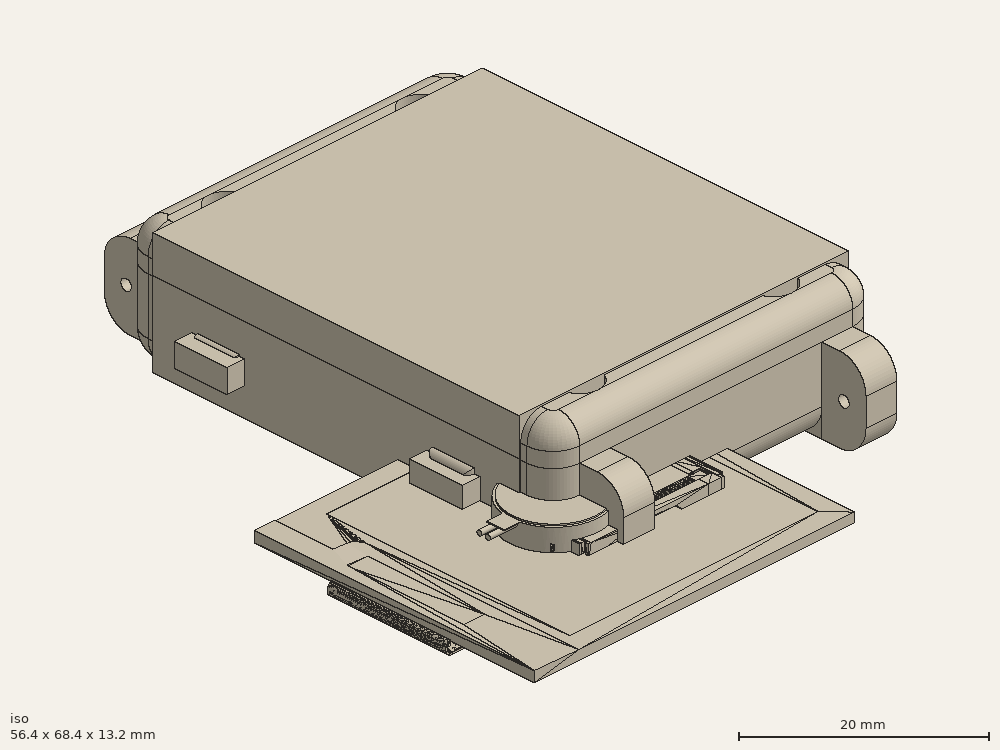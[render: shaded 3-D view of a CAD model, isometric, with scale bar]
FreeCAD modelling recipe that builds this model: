
FCSTD DOCUMENT  (FreeCAD 0.20R29177 +426 (Git))
Label: JJ-WATCHY_X
License: All rights reserved
LicenseURL: http://en.wikipedia.org/wiki/All_rights_reserved
objects: Part::Feature×73, App::Part×71, Sketcher::SketchObject×44, PartDesign::Pad×29, PartDesign::Pocket×23, PartDesign::ShapeBinder×11, PartDesign::Fillet×10, PartDesign::Body×8, PartDesign::Plane×4, Part::Part2DObjectPython×1, Part::Extrusion×1, PartDesign::FeatureBase×1, Mesh::Feature×1, Part::Fuse×1, Part::Cut×1
note: 269 computed .brp shape members not serialized (recipe doc carries the construction recipe); baked Part::Feature solids carry a one-line shape summary decoded from their .brp

FEATURE [Part::Feature] Part__Feature  label="SOLID (15)"
  shape: bbox 7.981 x 5.422 x 2.941 mm, 498 faces (baked)
FEATURE [App::Part] USB_Micro_B_Molex_47346_0001  label="USB_Micro-B_Molex_47346-0001"
  Group = -> [Part__Feature]
  Origin = -> Origin
  Placement = pos=(31.38,22.43,1.65) rot=(0,0,1;1.5708rad)
FEATURE [Part::Feature] Part__Feature001  label="SOLID"
  shape: bbox 1.6 x 0.8 x 0.8 mm, 28 faces (baked)
FEATURE [App::Part] C_0603_1608Metric
  Group = -> [Part__Feature001]
  Origin = -> Origin001
  Placement = pos=(5.16,37.71,1.65) rot=(0,0,1;0rad)
FEATURE [Part::Feature] Part__Feature002  label="SOLID (16)"
  shape: bbox 6.669 x 4.906 x 2.452 mm, 452 faces (baked)
FEATURE [App::Part] Button
  Group = -> [Part__Feature002]
  Origin = -> Origin002
  Placement = pos=(2.38,35.43,1.65) rot=(0,0,-1;1.5708rad)
FEATURE [Part::Feature] Part__Feature003  label="SOLID (16)001"
  shape: bbox 6.669 x 4.906 x 2.452 mm, 452 faces (baked)
FEATURE [App::Part] Button001
  Group = -> [Part__Feature003]
  Origin = -> Origin003
  Placement = pos=(2.38,8.73,1.65) rot=(0,0,-1;1.5708rad)
FEATURE [Part::Feature] Part__Feature004  label="SOLID (16)002"
  shape: bbox 6.669 x 4.906 x 2.452 mm, 452 faces (baked)
FEATURE [App::Part] Button002
  Group = -> [Part__Feature004]
  Origin = -> Origin004
  Placement = pos=(31.42,37.23,1.65) rot=(0,0,1;1.5708rad)
FEATURE [Part::Feature] Part__Feature005  label="SOLID (16)003"
  shape: bbox 6.669 x 4.906 x 2.452 mm, 452 faces (baked)
FEATURE [App::Part] Button003
  Group = -> [Part__Feature005]
  Origin = -> Origin005
  Placement = pos=(31.42,10.53,1.65) rot=(0,0,1;1.5708rad)
FEATURE [Part::Feature] Part__Feature006  label="SOLID (1)"
  shape: bbox 2 x 2 x 1.025 mm, 68 faces (baked)
FEATURE [App::Part] LGA_12_2x2mm_P0_5mm  label="LGA-12_2x2mm_P0.5mm"
  Group = -> [Part__Feature006]
  Origin = -> Origin006
  Placement = pos=(10.76,34.89,1.65) rot=(0,0,1;3.14159rad)
FEATURE [Part::Feature] Part__Feature007  label="COMPOUND (3)"
  shape: bbox 16.3 x 5.85 x 2.11 mm, 1280 faces, 17 solids (baked)
FEATURE [App::Part] FPC_24  label="FPC-24"
  Group = -> [Part__Feature007]
  Origin = -> Origin007
  Placement = pos=(11.025,19.09,1.65) rot=(0,0,1;0rad)
FEATURE [Part::Feature] Part__Feature008  label="SOLID (4)"
  shape: bbox 7.65 x 5.2 x 3.4 mm, 136 faces (baked)
FEATURE [App::Part] Molex_PicoBlade_53261_0271_1x02_1MP_P1_25mm_Horizontal  label="Molex_PicoBlade_53261-0271_1x02-1MP_P1.25mm_Horizontal"
  Group = -> [Part__Feature008]
  Origin = -> Origin008
  Placement = pos=(28.63,31.39,1.65) rot=(0,0,-1;1.5708rad)
FEATURE [Part::Feature] Part__Feature009  label="SOLID (2)"
  shape: bbox 1 x 0.5 x 0.35 mm, 26 faces (baked)
FEATURE [App::Part] R_0402_1005Metric
  Group = -> [Part__Feature009]
  Origin = -> Origin009
  Placement = pos=(31.7,28.28,1.65) rot=(0,0,1;1.5708rad)
FEATURE [Part::Feature] Part__Feature010  label="SOLID (5)"
  shape: bbox 4 x 4 x 1.1 mm, 158 faces (baked)
FEATURE [App::Part] QFN_24_1EP_4x4mm_P0_5mm_EP2_7x2_7mm  label="QFN-24-1EP_4x4mm_P0.5mm_EP2.7x2.7mm"
  Group = -> [Part__Feature010]
  Origin = -> Origin010
  Placement = pos=(25.76,24.38,1.65) rot=(0,0,1;0rad)
FEATURE [Part::Feature] Part__Feature011  label="SOLID (2)001"
  shape: bbox 1 x 0.5 x 0.35 mm, 26 faces (baked)
FEATURE [App::Part] R_0402_1005Metric001
  Group = -> [Part__Feature011]
  Origin = -> Origin011
  Placement = pos=(29.05,13.07,1.65) rot=(0,0,1;0rad)
FEATURE [Part::Feature] Part__Feature012  label="SOLID001"
  shape: bbox 1.6 x 0.8 x 0.8 mm, 28 faces (baked)
FEATURE [App::Part] C_0603_1608Metric001
  Group = -> [Part__Feature012]
  Origin = -> Origin012
  Placement = pos=(21.71,23.42,1.65) rot=(0,0,1;0rad)
FEATURE [Part::Feature] Part__Feature013  label="COMPOUND"
  shape: bbox 37.16 x 32.08 x 2.7 mm, 57 faces, 2 solids (baked)
FEATURE [App::Part] Display
  Group = -> [Part__Feature013]
  Origin = -> Origin013
  Placement = pos=(16.89,23.15,0.55) rot=(0.707107,0.707107,0;3.14159rad)
FEATURE [Part::Feature] Part__Feature014  label="SOLID002"
  shape: bbox 1.6 x 0.8 x 0.8 mm, 28 faces (baked)
FEATURE [App::Part] C_0603_1608Metric002
  Group = -> [Part__Feature014]
  Origin = -> Origin014
  Placement = pos=(15.42,35.06,1.65) rot=(0,0,1;1.5708rad)
FEATURE [Part::Feature] Part__Feature015  label="SOLID003"
  shape: bbox 1.6 x 0.8 x 0.8 mm, 28 faces (baked)
FEATURE [App::Part] C_0603_1608Metric003
  Group = -> [Part__Feature015]
  Origin = -> Origin015
  Placement = pos=(19.01,21.47,1.65) rot=(0,0,1;1.5708rad)
FEATURE [Part::Feature] Part__Feature016  label="SOLID (3)"
  shape: bbox 2 x 1.25 x 1.25 mm, 28 faces (baked)
FEATURE [App::Part] C_0805_2012Metric
  Group = -> [Part__Feature016]
  Origin = -> Origin016
  Placement = pos=(5.63,12.59,1.65) rot=(0,0,1;0rad)
FEATURE [Part::Feature] Part__Feature017  label="SOLID (3)001"
  shape: bbox 2 x 1.25 x 1.25 mm, 28 faces (baked)
FEATURE [App::Part] C_0805_2012Metric001
  Group = -> [Part__Feature017]
  Origin = -> Origin017
  Placement = pos=(6.63,6.34,1.65) rot=(0,0,1;0rad)
FEATURE [Part::Feature] Part__Feature018  label="SOLID004"
  shape: bbox 1.6 x 0.8 x 0.8 mm, 28 faces (baked)
FEATURE [App::Part] C_0603_1608Metric004
  Group = -> [Part__Feature018]
  Origin = -> Origin018
  Placement = pos=(13.81,21.47,1.65) rot=(0,0,1;1.5708rad)
FEATURE [Part::Feature] Part__Feature019  label="SOLID005"
  shape: bbox 1.6 x 0.8 x 0.8 mm, 28 faces (baked)
FEATURE [App::Part] C_0603_1608Metric005
  Group = -> [Part__Feature019]
  Origin = -> Origin019
  Placement = pos=(16.41,21.47,1.65) rot=(0,0,1;1.5708rad)
FEATURE [Part::Feature] Part__Feature020  label="SOLID006"
  shape: bbox 1.6 x 0.8 x 0.8 mm, 28 faces (baked)
FEATURE [App::Part] C_0603_1608Metric006
  Group = -> [Part__Feature020]
  Origin = -> Origin020
  Placement = pos=(17.71,21.47,1.65) rot=(0,0,1;1.5708rad)
FEATURE [Part::Feature] Part__Feature021  label="SOLID007"
  shape: bbox 1.6 x 0.8 x 0.8 mm, 28 faces (baked)
FEATURE [App::Part] C_0603_1608Metric007
  Group = -> [Part__Feature021]
  Origin = -> Origin021
  Placement = pos=(15.11,21.47,1.65) rot=(0,0,1;1.5708rad)
FEATURE [Part::Feature] Part__Feature022  label="SOLID008"
  shape: bbox 1.6 x 0.8 x 0.8 mm, 28 faces (baked)
FEATURE [App::Part] C_0603_1608Metric008
  Group = -> [Part__Feature022]
  Origin = -> Origin022
  Placement = pos=(12.46,21.47,1.65) rot=(0,0,1;1.5708rad)
FEATURE [Part::Feature] Part__Feature023  label="SOLID009"
  shape: bbox 1.6 x 0.8 x 0.8 mm, 28 faces (baked)
FEATURE [App::Part] C_0603_1608Metric009
  Group = -> [Part__Feature023]
  Origin = -> Origin023
  Placement = pos=(11.16,21.47,1.65) rot=(0,0,1;1.5708rad)
FEATURE [Part::Feature] Part__Feature024  label="SOLID (3)002"
  shape: bbox 2 x 1.25 x 1.25 mm, 28 faces (baked)
FEATURE [App::Part] C_0805_2012Metric002
  Group = -> [Part__Feature024]
  Origin = -> Origin024
  Placement = pos=(17.82,35.53,1.65) rot=(0,0,1;3.14159rad)
FEATURE [Part::Feature] Part__Feature025  label="SOLID (6)"
  shape: bbox 3.8 x 1.6 x 1.25 mm, 67 faces (baked)
FEATURE [App::Part] D_SOD_123  label="D_SOD-123"
  Group = -> [Part__Feature025]
  Origin = -> Origin025
  Placement = pos=(1.25,15.82,1.65) rot=(0,0,1;1.5708rad)
FEATURE [Part::Feature] Part__Feature026  label="SOLID (6)001"
  shape: bbox 3.8 x 1.6 x 1.25 mm, 67 faces (baked)
FEATURE [App::Part] D_SOD_123001  label="D_SOD-124"
  Group = -> [Part__Feature026]
  Origin = -> Origin026
  Placement = pos=(3.55,15.82,1.65) rot=(0,0,-1;1.5708rad)
FEATURE [Part::Feature] Part__Feature027  label="SOLID (6)002"
  shape: bbox 3.8 x 1.6 x 1.25 mm, 67 faces (baked)
FEATURE [App::Part] D_SOD_123002  label="D_SOD-125"
  Group = -> [Part__Feature027]
  Origin = -> Origin027
  Placement = pos=(5.85,15.82,1.65) rot=(0,0,-1;1.5708rad)
FEATURE [Part::Feature] Part__Feature028  label="SOLID (6)003"
  shape: bbox 3.8 x 1.6 x 1.25 mm, 67 faces (baked)
FEATURE [App::Part] D_SOD_123003  label="D_SOD-126"
  Group = -> [Part__Feature028]
  Origin = -> Origin028
  Placement = pos=(27.27,19.28,1.65) rot=(0,0,1;1.5708rad)
FEATURE [Part::Feature] Part__Feature029  label="SOLID (7)"
  shape: bbox 1.6 x 0.8 x 1.1 mm, 50 faces (baked)
FEATURE [App::Part] LED_0603_1608Metric
  Group = -> [Part__Feature029]
  Origin = -> Origin029
  Placement = pos=(33.04,30.53,1.65) rot=(0,0,1;1.5708rad)
FEATURE [Part::Feature] Part__Feature030  label="SOLID (8)"
  shape: bbox 3.5 x 1.6 x 1.1 mm, 27 faces (baked)
FEATURE [App::Part] D_SOD_123F  label="D_SOD-123F"
  Group = -> [Part__Feature030]
  Origin = -> Origin030
  Placement = pos=(4.91,34.705,1.65) rot=(0,0,-1;1.5708rad)
FEATURE [Part::Feature] Part__Feature031  label="SOLID (9)"
  shape: bbox 3.2 x 2.5 x 2.5 mm, 28 faces (baked)
FEATURE [App::Part] L_1210_3225Metric
  Group = -> [Part__Feature031]
  Origin = -> Origin031
  Placement = pos=(6.13,9.47,1.65) rot=(0,0,-1;1.5708rad)
FEATURE [Part::Feature] Part__Feature032  label="SOLID (10)"
  shape: bbox 2.5 x 3 x 1.2 mm, 76 faces (baked)
FEATURE [App::Part] SOT_23  label="SOT-23"
  Group = -> [Part__Feature032]
  Origin = -> Origin032
  Placement = pos=(28.1,9.03,1.65) rot=(0,0,-1;1.5708rad)
FEATURE [Part::Feature] Part__Feature033  label="SOLID (10)001"
  shape: bbox 2.5 x 3 x 1.2 mm, 76 faces (baked)
FEATURE [App::Part] SOT_23001  label="SOT-024"
  Group = -> [Part__Feature033]
  Origin = -> Origin033
  Placement = pos=(28.45,15.23,1.65) rot=(0,0,-1;1.5708rad)
FEATURE [Part::Feature] Part__Feature034  label="SOLID (10)002"
  shape: bbox 2.5 x 3 x 1.2 mm, 76 faces (baked)
FEATURE [App::Part] SOT_23002  label="SOT-025"
  Group = -> [Part__Feature034]
  Origin = -> Origin034
  Placement = pos=(7.81,35.31,1.65) rot=(0,0,1;3.14159rad)
FEATURE [Part::Feature] Part__Feature035  label="SOLID (2)002"
  shape: bbox 1 x 0.5 x 0.35 mm, 26 faces (baked)
FEATURE [App::Part] R_0402_1005Metric002
  Group = -> [Part__Feature035]
  Origin = -> Origin035
  Placement = pos=(16.97,34.19,1.65) rot=(0,0,1;3.14159rad)
FEATURE [Part::Feature] Part__Feature036  label="SOLID (2)003"
  shape: bbox 1 x 0.5 x 0.35 mm, 26 faces (baked)
FEATURE [App::Part] R_0402_1005Metric003
  Group = -> [Part__Feature036]
  Origin = -> Origin036
  Placement = pos=(22.55,26.67,1.65) rot=(0,0,1;1.5708rad)
FEATURE [Part::Feature] Part__Feature037  label="SOLID (2)004"
  shape: bbox 1 x 0.5 x 0.35 mm, 26 faces (baked)
FEATURE [App::Part] R_0402_1005Metric004
  Group = -> [Part__Feature037]
  Origin = -> Origin037
  Placement = pos=(23.91,27.48,1.65) rot=(0,0,1;3.14159rad)
FEATURE [Part::Feature] Part__Feature038  label="SOLID (2)005"
  shape: bbox 1 x 0.5 x 0.35 mm, 26 faces (baked)
FEATURE [App::Part] R_0402_1005Metric005
  Group = -> [Part__Feature038]
  Origin = -> Origin038
  Placement = pos=(27.15,13.07,1.65) rot=(0,0,1;3.14159rad)
FEATURE [Part::Feature] Part__Feature039  label="SOLID (2)006"
  shape: bbox 1 x 0.5 x 0.35 mm, 26 faces (baked)
FEATURE [App::Part] R_0402_1005Metric006
  Group = -> [Part__Feature039]
  Origin = -> Origin039
  Placement = pos=(28.66,36.44,1.65) rot=(0,0,1;0rad)
FEATURE [Part::Feature] Part__Feature040  label="SOLID (2)007"
  shape: bbox 1 x 0.5 x 0.35 mm, 26 faces (baked)
FEATURE [App::Part] R_0402_1005Metric007
  Group = -> [Part__Feature040]
  Origin = -> Origin040
  Placement = pos=(6.69,32.68,1.65) rot=(0,0,-1;1.5708rad)
FEATURE [Part::Feature] Part__Feature041  label="SOLID (2)008"
  shape: bbox 1 x 0.5 x 0.35 mm, 26 faces (baked)
FEATURE [App::Part] R_0402_1005Metric008
  Group = -> [Part__Feature041]
  Origin = -> Origin041
  Placement = pos=(29.05,11.28,1.65) rot=(0,0,1;3.14159rad)
FEATURE [Part::Feature] Part__Feature042  label="SOLID (2)009"
  shape: bbox 1 x 0.5 x 0.35 mm, 26 faces (baked)
FEATURE [App::Part] R_0402_1005Metric009
  Group = -> [Part__Feature042]
  Origin = -> Origin042
  Placement = pos=(27.15,11.28,1.65) rot=(0,0,1;3.14159rad)
FEATURE [Part::Feature] Part__Feature043  label="SOLID (2)010"
  shape: bbox 1 x 0.5 x 0.35 mm, 26 faces (baked)
FEATURE [App::Part] R_0402_1005Metric010
  Group = -> [Part__Feature043]
  Origin = -> Origin043
  Placement = pos=(4.35,6.34,1.65) rot=(0,0,1;1.5708rad)
FEATURE [Part::Feature] Part__Feature044  label="SOLID (2)011"
  shape: bbox 1 x 0.5 x 0.35 mm, 26 faces (baked)
FEATURE [App::Part] R_0402_1005Metric011
  Group = -> [Part__Feature044]
  Origin = -> Origin044
  Placement = pos=(30.8,28.28,1.65) rot=(0,0,1;1.5708rad)
FEATURE [Part::Feature] Part__Feature045  label="SOLID (2)012"
  shape: bbox 1 x 0.5 x 0.35 mm, 26 faces (baked)
FEATURE [App::Part] R_0402_1005Metric012
  Group = -> [Part__Feature045]
  Origin = -> Origin045
  Placement = pos=(29.32,17.4,1.65) rot=(0,0,1;3.14159rad)
FEATURE [Part::Feature] Part__Feature046  label="SOLID (2)013"
  shape: bbox 1 x 0.5 x 0.35 mm, 26 faces (baked)
FEATURE [App::Part] R_0402_1005Metric013
  Group = -> [Part__Feature046]
  Origin = -> Origin046
  Placement = pos=(33.24,28.28,1.65) rot=(0,0,-1;1.5708rad)
FEATURE [Part::Feature] Part__Feature047  label="SOLID (2)014"
  shape: bbox 1 x 0.5 x 0.35 mm, 26 faces (baked)
FEATURE [App::Part] R_0402_1005Metric014
  Group = -> [Part__Feature047]
  Origin = -> Origin047
  Placement = pos=(7.75,32.68,1.65) rot=(0,0,-1;1.5708rad)
FEATURE [Part::Feature] Part__Feature048  label="SOLID (13)"
  shape: bbox 7 x 7 x 0.77 mm, 302 faces (baked)
FEATURE [App::Part] QFN_48_1EP_7x7mm_P0_5mm_EP5_15x5_15mm  label="QFN-48-1EP_7x7mm_P0.5mm_EP5.15x5.15mm"
  Group = -> [Part__Feature048]
  Origin = -> Origin048
  Placement = pos=(17.7737,29.6588,1.65) rot=(0,0,-1;1.5708rad)
FEATURE [Part::Feature] Part__Feature049  label="SOLID (11)"
  shape: bbox 2.8 x 2.9 x 1.55 mm, 109 faces (baked)
FEATURE [App::Part] SOT_23_5  label="SOT-23-5"
  Group = -> [Part__Feature049]
  Origin = -> Origin049
  Placement = pos=(24.66,19.88,1.65) rot=(0,0,-1;1.5708rad)
FEATURE [Part::Feature] Part__Feature050  label="SOLID (11)001"
  shape: bbox 2.8 x 2.9 x 1.55 mm, 109 faces (baked)
FEATURE [App::Part] SOT_23_5001  label="SOT-23-006"
  Group = -> [Part__Feature050]
  Origin = -> Origin050
  Placement = pos=(32,15.93,1.65) rot=(0,0,-1;1.5708rad)
FEATURE [Part::Feature] Part__Feature051  label="SOLID (12)"
  shape: bbox 2 x 2 x 1.05 mm, 118 faces (baked)
FEATURE [App::Part] SOT_363_SC_70_6  label="SOT-363_SC-70-6"
  Group = -> [Part__Feature051]
  Origin = -> Origin051
  Placement = pos=(21.31,21.47,1.65) rot=(0,0,1;3.14159rad)
FEATURE [Part::Feature] Part__Feature052  label="SOLID (14)"
  shape: bbox 6 x 4.9 x 1.75 mm, 156 faces (baked)
FEATURE [App::Part] SOIC_8_3_9x4_9mm_P1_27mm  label="SOIC-8_3.9x4.9mm_P1.27mm"
  Group = -> [Part__Feature052]
  Origin = -> Origin052
  Placement = pos=(11.07,29.81,1.65) rot=(0,0,1;1.5708rad)
FEATURE [Part::Feature] Part__Feature053  label="SOLID (2)015"
  shape: bbox 1 x 0.5 x 0.35 mm, 26 faces (baked)
FEATURE [App::Part] R_0402_1005Metric015
  Group = -> [Part__Feature053]
  Origin = -> Origin053
  Placement = pos=(7.75,30.52,1.65) rot=(0,0,-1;1.5708rad)
FEATURE [Part::Feature] Part__Feature054  label="COMPOUND (1)"
  shape: bbox 13 x 10 x 2.5 mm, 15 faces, 3 solids (baked)
FEATURE [App::Part] PagerMotor
  Group = -> [Part__Feature054]
  Origin = -> Origin054
  Placement = pos=(5.45,22.955,5.15) rot=(0.819152,-0.573576,0;3.14159rad)
FEATURE [Part::Feature] Part__Feature055  label="COMPOUND (2)"
  shape: bbox 33.8 x 45.96 x 1 mm, 46 faces (baked)
FEATURE [App::Part] Watchy_Fixed_Dimensions_v1  label="Watchy Fixed Dimensions v1"
  Group = -> [USB_Micro_B_Molex_47346_0001,C_0603_1608Metric,Button,Button001,Button002,Button003,LGA_12_2x2mm_P0_5mm,FPC_24,Molex_PicoBlade_53261_0271_1x02_1MP_P1_25mm_Horizontal,R_0402_1005Metric,QFN_24_1EP_4x4mm_P0_5mm_EP2_7x2_7mm,R_0402_1005Metric001,C_0603_1608Metric001,Display,C_0603_1608Metric002,C_0603_1608Metric003,C_0805_2012Metric,C_0805_2012Metric001,C_0603_1608Metric004,C_0603_1608Metric005,+36 more]
  Origin = -> Origin055
  Placement = pos=(0,0,-0.43) rot=(0,0,1;0rad)
FEATURE [Sketcher::SketchObject] Sketch
  FullyConstrained = true
  MapMode = 5
  Placement = pos=(0,0,0) rot=(0,1,0;3.14159rad)
  Support = -> [XY_Plane056]
  sketch-geometry (4):
    g0: LineSegment StartX=-32.81 StartY=41.31 StartZ=0 EndX=-0.98 EndY=41.31 EndZ=0
    g1: LineSegment StartX=-0.98 StartY=41.31 StartZ=0 EndX=-0.98 EndY=10.07 EndZ=0
    g2: LineSegment StartX=-0.98 StartY=10.07 StartZ=0 EndX=-32.81 EndY=10.07 EndZ=0
    g3: LineSegment StartX=-32.81 StartY=10.07 StartZ=0 EndX=-32.81 EndY=41.31 EndZ=0
  constraints (12):
    c: Coincident(g0,g1)
    c: Coincident(g1,g2)
    c: Coincident(g2,g3)
    c: Coincident(g3,g0)
    c: Horizontal(g0)
    c: Horizontal(g2)
    c: Vertical(g1)
    c: Vertical(g3)
    c: DistanceX(g0,g0) = 31.83
    c: DistanceY(g1,g1) = 31.24
    c: DistanceY(g-1,g1) = 10.07
    c: DistanceX(g1,g-1) = 0.98
FEATURE [PartDesign::Pad] Pad
  Direction = (0,0,-1)
  Length = 1.5
  Length2 = 10
  Profile = -> Sketch
  ReferenceAxis = -> Sketch [N_Axis]
  Type = 0
FEATURE [PartDesign::Fillet] Fillet
  Base = -> Pad [Edge1,Edge2,Edge5,Edge8]
  BaseFeature = -> Pad
  Radius = 1
  SupportTransform = false
  UseAllEdges = false
FEATURE [PartDesign::Pocket] Pocket
  BaseFeature = -> Fillet
  Direction = (0,0,-1)
  Length = 0.9
  Length2 = 5
  Profile = -> Fillet [Face2]
  Type = 0
FEATURE [PartDesign::ShapeBinder] ReferencePocket
  Placement = pos=(0,0,-1.5) rot=(0,0,1;0rad)
  Support = -> [Pocket]
  TraceSupport = false
FEATURE [PartDesign::Plane] DatumPlane
  Length = 75.1964
  MapMode = 5
  Placement = pos=(0,0,-1.5) rot=(1,0,0;3.14159rad)
  ResizeMode = 0
  Support = -> [ReferencePocket]
  Width = 91.2964
FEATURE [Sketcher::SketchObject] Sketch001
  ExternalGeometry = -> [ReferencePocket]
  FullyConstrained = true
  MapMode = 5
  Placement = pos=(0,0,-1.5) rot=(1,0,0;3.14159rad)
  Support = -> [DatumPlane]
  sketch-geometry (5):
    g0: LineSegment StartX=-1.6 StartY=1.5 StartZ=0 EndX=35.4 EndY=1.5 EndZ=0
    g1: LineSegment StartX=35.4 StartY=1.5 StartZ=0 EndX=35.4 EndY=-47.5 EndZ=0
    g2: LineSegment StartX=35.4 StartY=-47.5 StartZ=0 EndX=-1.6 EndY=-47.5 EndZ=0
    g3: LineSegment StartX=-1.6 StartY=-47.5 StartZ=0 EndX=-1.6 EndY=1.5 EndZ=0
    g4: GeomPoint X=16.9 Y=-23 Z=0
  constraints (13):
    c: Coincident(g0,g1)
    c: Coincident(g1,g2)
    c: Coincident(g2,g3)
    c: Coincident(g3,g0)
    c: Horizontal(g0)
    c: Horizontal(g2)
    c: Vertical(g1)
    c: Vertical(g3)
    c: DistanceX(g0,g0) = 37
    c: DistanceY(g1,g1) = 49
    c: DistanceX(g-1,g4) = 16.9
    c: DistanceY(g4,g-1) = 23
    c: Symmetric(g2,g0,g4)
FEATURE [PartDesign::Pad] Pad001
  Direction = (0,0,-1)
  Length = 1
  Length2 = 8
  Placement = pos=(0,0,-1.5) rot=(1,0,0;3.14159rad)
  Profile = -> Sketch001
  ReferenceAxis = -> Sketch001 [N_Axis]
  Type = 4
FEATURE [Sketcher::SketchObject] Sketch002
  FullyConstrained = true
  MapMode = 5
  Placement = pos=(0,0,-2.5) rot=(1,0,0;3.14159rad)
  Support = -> [Pad001]
  sketch-geometry (5):
    g0: LineSegment StartX=3 StartY=-12.3 StartZ=0 EndX=31 EndY=-12.3 EndZ=0
    g1: LineSegment StartX=31 StartY=-12.3 StartZ=0 EndX=31 EndY=-39.3 EndZ=0
    g2: LineSegment StartX=31 StartY=-39.3 StartZ=0 EndX=3 EndY=-39.3 EndZ=0
    g3: LineSegment StartX=3 StartY=-39.3 StartZ=0 EndX=3 EndY=-12.3 EndZ=0
    g4: GeomPoint X=17 Y=-25.8 Z=0
  constraints (13):
    c: Coincident(g0,g1)
    c: Coincident(g1,g2)
    c: Coincident(g2,g3)
    c: Coincident(g3,g0)
    c: Horizontal(g0)
    c: Horizontal(g2)
    c: Vertical(g1)
    c: Vertical(g3)
    c: DistanceX(g0,g0) = 28
    c: DistanceY(g1,g1) = 27
    c: DistanceX(g-1,g4) = 17
    c: DistanceY(g4,g-1) = 25.8
    c: Symmetric(g2,g0,g4)
FEATURE [PartDesign::Pocket] Pocket001
  BaseFeature = -> Pad001
  Direction = (0,-1e-16,1)
  Length = 1
  Length2 = 5
  Placement = pos=(0,0,-1.5) rot=(1,0,0;3.14159rad)
  Profile = -> Sketch002
  ReferenceAxis = -> Sketch002 [N_Axis]
  Type = 0
FEATURE [Sketcher::SketchObject] Sketch003
  ExternalGeometry = -> [Pocket001]
  FullyConstrained = true
  MapMode = 5
  Placement = pos=(0,0,6.5) rot=(0,0,1;0rad)
  Support = -> [Pocket001]
  sketch-geometry (5):
    g0: LineSegment StartX=-0.6 StartY=46.5 StartZ=0 EndX=-0.6 EndY=-0.5 EndZ=0
    g1: LineSegment StartX=-0.6 StartY=-0.5 StartZ=0 EndX=34.4 EndY=-0.5 EndZ=0
    g2: LineSegment StartX=34.4 StartY=-0.5 StartZ=0 EndX=34.4 EndY=46.5 EndZ=0
    g3: LineSegment StartX=34.4 StartY=46.5 StartZ=0 EndX=-0.6 EndY=46.5 EndZ=0
    g4: Circle CenterX=16.9 CenterY=23 CenterZ=0 NormalX=0 NormalY=0 NormalZ=1 AngleXU=0 Radius=29.3002
  constraints (14):
    c: Coincident(g0,g1)
    c: Coincident(g1,g2)
    c: Coincident(g2,g3)
    c: Coincident(g3,g0)
    c: PointOnObject(g0,g4)
    c: PointOnObject(g1,g4)
    c: PointOnObject(g2,g4)
    c: PointOnObject(g3,g4)
    c: Horizontal(g3)
    c: Horizontal(g1)
    c: Vertical(g2)
    c: DistanceX(g3,g3) = 35
    c: DistanceY(g2,g2) = 47
    c: Symmetric(g-3,g-4,g4)
FEATURE [PartDesign::Pocket] Pocket002
  BaseFeature = -> Pocket001
  Direction = (0,2e-16,-1)
  Length = 7
  Length2 = 5
  Placement = pos=(0,0,-1.5) rot=(1,0,0;3.14159rad)
  Profile = -> Sketch003
  ReferenceAxis = -> Sketch003 [N_Axis]
  Type = 0
FEATURE [Sketcher::SketchObject] Sketch004
  ExternalGeometry = -> [ReferencePocket]
  FullyConstrained = true
  MapMode = 5
  Placement = pos=(0,-2e-16,-0.5) rot=(0,0,1;0rad)
  Support = -> [Pocket002]
  sketch-geometry (4):
    g0: LineSegment StartX=0.48 StartY=41.81 StartZ=0 EndX=33.31 EndY=41.81 EndZ=0
    g1: LineSegment StartX=33.31 StartY=41.81 StartZ=0 EndX=33.31 EndY=9.57 EndZ=0
    g2: LineSegment StartX=33.31 StartY=9.57 StartZ=0 EndX=0.48 EndY=9.57 EndZ=0
    g3: LineSegment StartX=0.48 StartY=9.57 StartZ=0 EndX=0.48 EndY=41.81 EndZ=0
  constraints (12):
    c: Coincident(g0,g1)
    c: Coincident(g1,g2)
    c: Coincident(g2,g3)
    c: Coincident(g3,g0)
    c: Horizontal(g0)
    c: Horizontal(g2)
    c: Vertical(g1)
    c: Vertical(g3)
    c: DistanceX(g0,g-4) = 0.5
    c: DistanceX(g-6,g0) = 0.5
    c: DistanceY(g-3,g0) = 0.5
    c: DistanceY(g1,g-5) = 0.5
FEATURE [PartDesign::Pocket] Pocket003
  BaseFeature = -> Pocket002
  Direction = (0,4e-16,-1)
  Length = 1
  Length2 = 5
  Placement = pos=(0,0,-1.5) rot=(1,0,0;3.14159rad)
  Profile = -> Sketch004
  ReferenceAxis = -> Sketch004 [N_Axis]
  Type = 0
FEATURE [Sketcher::SketchObject] Sketch005
  FullyConstrained = true
  MapMode = 5
  Placement = pos=(34.4,0,-1.5) rot=(0.57735,0.57735,-0.57735;4.18879rad)
  Support = -> [Pocket003]
  sketch-geometry (4):
    g0: LineSegment StartX=18.2 StartY=-2.15 StartZ=0 EndX=26.7 EndY=-2.15 EndZ=0
    g1: LineSegment StartX=26.7 StartY=-2.15 StartZ=0 EndX=26.7 EndY=-5.75 EndZ=0
    g2: LineSegment StartX=26.7 StartY=-5.75 StartZ=0 EndX=18.2 EndY=-5.75 EndZ=0
    g3: LineSegment StartX=18.2 StartY=-5.75 StartZ=0 EndX=18.2 EndY=-2.15 EndZ=0
  constraints (12):
    c: Coincident(g0,g1)
    c: Coincident(g1,g2)
    c: Coincident(g2,g3)
    c: Coincident(g3,g0)
    c: Horizontal(g0)
    c: Horizontal(g2)
    c: Vertical(g1)
    c: Vertical(g3)
    c: DistanceX(g2,g2) = 8.5
    c: DistanceY(g1,g1) = 3.6
    c: DistanceX(g-1,g0) = 18.2
    c: DistanceY(g0,g-1) = 2.15
FEATURE [PartDesign::Pocket] Pocket004
  BaseFeature = -> Pocket003
  Direction = (1,0,0)
  Length = 5
  Length2 = 5
  Placement = pos=(0,0,-1.5) rot=(1,0,0;3.14159rad)
  Profile = -> Sketch005
  ReferenceAxis = -> Sketch005 [N_Axis]
  Type = 0
FEATURE [Sketcher::SketchObject] Sketch006
  ExternalGeometry = -> [Pocket004]
  FullyConstrained = true
  MapMode = 5
  Placement = pos=(0,0,6.5) rot=(0,0,1;0rad)
  Support = -> [Pocket004]
  sketch-geometry (20):
    g0: LineSegment StartX=-1 StartY=37.83 StartZ=0 EndX=-0.6 EndY=37.83 EndZ=0
    g1: LineSegment StartX=-0.6 StartY=37.83 StartZ=0 EndX=-0.6 EndY=34.83 EndZ=0
    g2: LineSegment StartX=-0.6 StartY=34.83 StartZ=0 EndX=-1 EndY=34.83 EndZ=0
    g3: LineSegment StartX=-1 StartY=34.83 StartZ=0 EndX=-1 EndY=37.83 EndZ=0
    g4: LineSegment StartX=34.4 StartY=37.83 StartZ=0 EndX=34.8 EndY=37.83 EndZ=0
    g5: LineSegment StartX=34.8 StartY=37.83 StartZ=0 EndX=34.8 EndY=34.83 EndZ=0
    g6: LineSegment StartX=34.8 StartY=34.83 StartZ=0 EndX=34.4 EndY=34.83 EndZ=0
    g7: LineSegment StartX=34.4 StartY=34.83 StartZ=0 EndX=34.4 EndY=37.83 EndZ=0
    g8: LineSegment StartX=34.4 StartY=8.13 StartZ=0 EndX=34.8 EndY=8.13 EndZ=0
    g9: LineSegment StartX=34.8 StartY=8.13 StartZ=0 EndX=34.8 EndY=11.13 EndZ=0
    g10: LineSegment StartX=34.8 StartY=11.13 StartZ=0 EndX=34.4 EndY=11.13 EndZ=0
    g11: LineSegment StartX=34.4 StartY=11.13 StartZ=0 EndX=34.4 EndY=8.13 EndZ=0
    g12: LineSegment StartX=-1 StartY=11.13 StartZ=0 EndX=-0.6 EndY=11.13 EndZ=0
    g13: LineSegment StartX=-0.6 StartY=11.13 StartZ=0 EndX=-0.6 EndY=8.13 EndZ=0
    g14: LineSegment StartX=-0.6 StartY=8.13 StartZ=0 EndX=-1 EndY=8.13 EndZ=0
    g15: LineSegment StartX=-1 StartY=8.13 StartZ=0 EndX=-1 EndY=11.13 EndZ=0
    g16: Circle CenterX=-0.8 CenterY=9.63 CenterZ=0 NormalX=0 NormalY=0 NormalZ=1 AngleXU=0 Radius=1.51327
    g17: Circle CenterX=34.6 CenterY=9.63 CenterZ=0 NormalX=0 NormalY=0 NormalZ=1 AngleXU=0 Radius=1.51327
    g18: Circle CenterX=34.6 CenterY=36.33 CenterZ=0 NormalX=0 NormalY=0 NormalZ=1 AngleXU=0 Radius=1.51327
    g19: Circle CenterX=-0.8 CenterY=36.33 CenterZ=0 NormalX=0 NormalY=0 NormalZ=1 AngleXU=0 Radius=1.51327
  constraints (60):
    c: Coincident(g0,g1)
    c: Coincident(g1,g2)
    c: Coincident(g2,g3)
    c: Coincident(g3,g0)
    c: Horizontal(g0)
    c: Horizontal(g2)
    c: Vertical(g1)
    c: Vertical(g3)
    c: PointOnObject(g0,g-3)
    c: DistanceX(g0,g0) = 0.4
    c: DistanceY(g3,g3) = 3
    c: Coincident(g4,g5)
    c: Coincident(g5,g6)
    c: Coincident(g6,g7)
    c: Coincident(g7,g4)
    c: Horizontal(g4)
    c: Horizontal(g6)
    c: Vertical(g5)
    c: Vertical(g7)
    c: Coincident(g8,g9)
    c: Coincident(g9,g10)
    c: Coincident(g10,g11)
    c: Coincident(g11,g8)
    c: Horizontal(g8)
    c: Horizontal(g10)
    c: Vertical(g9)
    c: Vertical(g11)
    c: Coincident(g12,g13)
    c: Coincident(g13,g14)
    c: Coincident(g14,g15)
    c: Coincident(g15,g12)
    c: Horizontal(g12)
    c: Horizontal(g14)
    c: Vertical(g13)
    c: Vertical(g15)
    c: Equal(g0,g12)
    c: Equal(g12,g4)
    c: Equal(g4,g8)
    c: Equal(g3,g13)
    c: Equal(g13,g5)
    c: Equal(g5,g9)
    c: PointOnObject(g12,g-3)
    c: PointOnObject(g4,g-4)
    c: PointOnObject(g8,g-4)
    c: PointOnObject(g12,g16)
    c: PointOnObject(g12,g16)
    c: PointOnObject(g14,g16)
    c: DistanceY(g-1,g16) = 9.63
    c: PointOnObject(g9,g17)
    c: PointOnObject(g10,g17)
    c: PointOnObject(g8,g17)
    c: PointOnObject(g4,g18)
    c: PointOnObject(g4,g18)
    c: PointOnObject(g5,g18)
    c: PointOnObject(g0,g19)
    c: PointOnObject(g0,g19)
    c: PointOnObject(g2,g19)
    c: DistanceY(g-1,g19) = 36.33
    c: DistanceY(g-1,g18) = 36.33
    c: DistanceY(g-1,g17) = 9.63
FEATURE [PartDesign::Pocket] Pocket005
  BaseFeature = -> Pocket004
  Direction = (0,0,-1)
  Length = 5.5
  Length2 = 5
  Placement = pos=(0,0,-1.5) rot=(1,0,0;3.14159rad)
  Profile = -> Sketch006
  ReferenceAxis = -> Sketch006 [N_Axis]
  Type = 0
FEATURE [Sketcher::SketchObject] Sketch007
  FullyConstrained = true
  MapMode = 5
  Placement = pos=(-1.6,0,-1.5) rot=(0.57735,0.57735,-0.57735;4.18879rad)
  Support = -> [Pocket005]
  sketch-geometry (8):
    g0: LineSegment StartX=7.23 StartY=-3.5 StartZ=0 EndX=12.03 EndY=-3.5 EndZ=0
    g1: LineSegment StartX=12.03 StartY=-3.5 StartZ=0 EndX=12.03 EndY=-5.3 EndZ=0
    g2: LineSegment StartX=12.03 StartY=-5.3 StartZ=0 EndX=7.23 EndY=-5.3 EndZ=0
    g3: LineSegment StartX=7.23 StartY=-5.3 StartZ=0 EndX=7.23 EndY=-3.5 EndZ=0
    g4: LineSegment StartX=33.9 StartY=-3.1 StartZ=0 EndX=38.7 EndY=-3.1 EndZ=0
    g5: LineSegment StartX=38.7 StartY=-3.1 StartZ=0 EndX=38.7 EndY=-4.9 EndZ=0
    g6: LineSegment StartX=38.7 StartY=-4.9 StartZ=0 EndX=33.9 EndY=-4.9 EndZ=0
    g7: LineSegment StartX=33.9 StartY=-4.9 StartZ=0 EndX=33.9 EndY=-3.1 EndZ=0
  constraints (24):
    c: Coincident(g0,g1)
    c: Coincident(g1,g2)
    c: Coincident(g2,g3)
    c: Coincident(g3,g0)
    c: Horizontal(g0)
    c: Horizontal(g2)
    c: Vertical(g1)
    c: Vertical(g3)
    c: Coincident(g4,g5)
    c: Coincident(g5,g6)
    c: Coincident(g6,g7)
    c: Coincident(g7,g4)
    c: Horizontal(g4)
    c: Horizontal(g6)
    c: Vertical(g5)
    c: Vertical(g7)
    c: DistanceX(g2,g2) = 4.8
    c: DistanceY(g1,g1) = 1.8
    c: Equal(g1,g7)
    c: Equal(g2,g6)
    c: DistanceY(g0,g-1) = 3.5
    c: DistanceY(g4,g-1) = 3.1
    c: DistanceX(g-1,g0) = 7.23
    c: DistanceX(g-1,g4) = 33.9
FEATURE [PartDesign::Pad] Pad002
  BaseFeature = -> Pocket005
  Direction = (-1,0,0)
  Length = 1
  Length2 = 10
  Placement = pos=(0,0,-1.5) rot=(1,0,0;3.14159rad)
  Profile = -> Sketch007
  ReferenceAxis = -> Sketch007 [N_Axis]
  Type = 0
FEATURE [Sketcher::SketchObject] Sketch008
  ExternalGeometry = -> [Pad002]
  FullyConstrained = true
  MapMode = 5
  Placement = pos=(35.4,0,-1.5) rot=(0.57735,-0.57735,0.57735;4.18879rad)
  Support = -> [Pad002]
  sketch-geometry (8):
    g0: LineSegment StartX=-12.03 StartY=-3.5 StartZ=0 EndX=-7.23 EndY=-3.5 EndZ=0
    g1: LineSegment StartX=-7.23 StartY=-3.5 StartZ=0 EndX=-7.23 EndY=-5.3 EndZ=0
    g2: LineSegment StartX=-7.23 StartY=-5.3 StartZ=0 EndX=-12.03 EndY=-5.3 EndZ=0
    g3: LineSegment StartX=-12.03 StartY=-5.3 StartZ=0 EndX=-12.03 EndY=-3.5 EndZ=0
    g4: LineSegment StartX=-38.7 StartY=-3.1 StartZ=0 EndX=-33.9 EndY=-3.1 EndZ=0
    g5: LineSegment StartX=-33.9 StartY=-3.1 StartZ=0 EndX=-33.9 EndY=-4.9 EndZ=0
    g6: LineSegment StartX=-33.9 StartY=-4.9 StartZ=0 EndX=-38.7 EndY=-4.9 EndZ=0
    g7: LineSegment StartX=-38.7 StartY=-4.9 StartZ=0 EndX=-38.7 EndY=-3.1 EndZ=0
  constraints (20):
    c: Coincident(g0,g1)
    c: Coincident(g1,g2)
    c: Coincident(g2,g3)
    c: Coincident(g3,g0)
    c: Horizontal(g0)
    c: Horizontal(g2)
    c: Vertical(g1)
    c: Vertical(g3)
    c: Coincident(g0,g-4)
    c: Coincident(g1,g-6)
    c: Coincident(g4,g5)
    c: Coincident(g5,g6)
    c: Coincident(g6,g7)
    c: Coincident(g7,g4)
    c: Horizontal(g4)
    c: Horizontal(g6)
    c: Vertical(g5)
    c: Vertical(g7)
    c: Coincident(g4,g-8)
    c: Coincident(g5,g-7)
FEATURE [PartDesign::Pad] Pad003
  BaseFeature = -> Pad002
  Direction = (1,0,0)
  Length = 1
  Length2 = 10
  Placement = pos=(0,0,-1.5) rot=(1,0,0;3.14159rad)
  Profile = -> Sketch008
  ReferenceAxis = -> Sketch008 [N_Axis]
  Type = 0
FEATURE [PartDesign::Fillet] Fillet001
  Base = -> Pad003 [Edge5,Edge105,Edge18,Edge124,Edge1,Edge2,Edge116,Edge103]
  BaseFeature = -> Pad003
  Placement = pos=(0,0,-1.5) rot=(1,0,0;3.14159rad)
  Radius = 3
  SupportTransform = false
  UseAllEdges = false
FEATURE [PartDesign::Fillet] Fillet002
  Base = -> Fillet001 [Edge41]
  BaseFeature = -> Fillet001
  Placement = pos=(0,0,-1.5) rot=(1,0,0;3.14159rad)
  Radius = 3
  SupportTransform = false
  UseAllEdges = false
FEATURE [PartDesign::Fillet] Fillet003
  Base = -> Fillet002 [Edge60,Edge59,Edge58,Edge61]
  BaseFeature = -> Fillet002
  Placement = pos=(0,0,-1.5) rot=(1,0,0;3.14159rad)
  Radius = 0.2
  SupportTransform = false
  UseAllEdges = false
FEATURE [PartDesign::ShapeBinder] ReferenceFillet003
  Placement = pos=(0,0,-1.5) rot=(1,0,0;3.14159rad)
  Support = -> [Fillet003]
  TraceSupport = false
FEATURE [PartDesign::Plane] DatumPlane001
  Length = 73.6348
  MapMode = 5
  Placement = pos=(0,0,6.5) rot=(0,0,1;0rad)
  ResizeMode = 0
  Support = -> [ReferenceFillet003]
  Width = 85.7348
FEATURE [Sketcher::SketchObject] Sketch009
  ExternalGeometry = -> [ReferenceFillet003]
  FullyConstrained = true
  MapMode = 5
  Placement = pos=(0,0,6.5) rot=(0,0,1;0rad)
  Support = -> [DatumPlane001]
  sketch-geometry (8):
    g0: LineSegment StartX=1.4 StartY=47.5 StartZ=0 EndX=32.4 EndY=47.5 EndZ=0
    g1: LineSegment StartX=-1.6 StartY=44.5 StartZ=0 EndX=-1.6 EndY=1.5 EndZ=0
    g2: LineSegment StartX=35.4 StartY=44.5 StartZ=0 EndX=35.4 EndY=1.5 EndZ=0
    g3: LineSegment StartX=1.4 StartY=-1.5 StartZ=0 EndX=32.4 EndY=-1.5 EndZ=0
    g4: ArcOfCircle CenterX=1.4 CenterY=1.5 CenterZ=0 NormalX=0 NormalY=0 NormalZ=1 AngleXU=0 Radius=3 StartAngle=3.14159 EndAngle=4.71239
    g5: ArcOfCircle CenterX=32.4 CenterY=1.5 CenterZ=0 NormalX=0 NormalY=0 NormalZ=1 AngleXU=0 Radius=3 StartAngle=4.71239 EndAngle=6.28319
    g6: ArcOfCircle CenterX=1.4 CenterY=44.5 CenterZ=0 NormalX=0 NormalY=0 NormalZ=1 AngleXU=0 Radius=3 StartAngle=1.5708 EndAngle=3.14159
    g7: ArcOfCircle CenterX=32.4 CenterY=44.5 CenterZ=0 NormalX=0 NormalY=0 NormalZ=1 AngleXU=0 Radius=3 StartAngle=3e-16 EndAngle=1.5708
  constraints (20):
    c: Coincident(g0,g-4)
    c: Coincident(g0,g-6)
    c: Coincident(g1,g-5)
    c: Coincident(g1,g-7)
    c: Coincident(g2,g-10)
    c: Coincident(g2,g-10)
    c: Coincident(g3,g-8)
    c: Coincident(g3,g-9)
    c: Coincident(g4,g-7)
    c: Coincident(g4,g1)
    c: Coincident(g4,g3)
    c: Coincident(g5,g-9)
    c: Coincident(g5,g2)
    c: Coincident(g5,g3)
    c: Coincident(g6,g-4)
    c: Coincident(g6,g1)
    c: Coincident(g6,g0)
    c: Coincident(g7,g-6)
    c: Coincident(g7,g0)
    c: Coincident(g7,g2)
FEATURE [PartDesign::Pad] Pad004
  Direction = (0,-4e-16,1)
  Length = 4
  Length2 = 10
  Placement = pos=(0,-2.9e-15,6.5) rot=(0,0,1;0rad)
  Profile = -> Sketch009
  ReferenceAxis = -> Sketch009 [N_Axis]
  Type = 0
FEATURE [PartDesign::Fillet] Fillet004
  Base = -> Pad004 [Edge7]
  BaseFeature = -> Pad004
  Placement = pos=(0,-2.9e-15,6.5) rot=(0,0,1;0rad)
  Radius = 2.4
  SupportTransform = false
  UseAllEdges = false
FEATURE [Sketcher::SketchObject] Sketch010
  ExternalGeometry = -> [ReferenceFillet003]
  FullyConstrained = true
  MapMode = 5
  Placement = pos=(0,-2.9e-15,6.5) rot=(1,0,0;3.14159rad)
  Support = -> [Fillet004]
  sketch-geometry (8):
    g0: ArcOfCircle CenterX=2.4 CenterY=-2.5 CenterZ=0 NormalX=0 NormalY=0 NormalZ=1 AngleXU=0 Radius=2 StartAngle=1.5708 EndAngle=3.14159
    g1: ArcOfCircle CenterX=31.4 CenterY=-2.5 CenterZ=0 NormalX=0 NormalY=0 NormalZ=1 AngleXU=0 Radius=2 StartAngle=0 EndAngle=1.5708
    g2: ArcOfCircle CenterX=31.4 CenterY=-43.5 CenterZ=0 NormalX=0 NormalY=0 NormalZ=1 AngleXU=0 Radius=2 StartAngle=4.71239 EndAngle=6.28319
    g3: ArcOfCircle CenterX=2.4 CenterY=-43.5 CenterZ=0 NormalX=0 NormalY=0 NormalZ=1 AngleXU=0 Radius=2 StartAngle=3.14159 EndAngle=4.7124
    g4: LineSegment StartX=0.4 StartY=-2.5 StartZ=0 EndX=0.4 EndY=-43.5 EndZ=0
    g5: LineSegment StartX=2.4 StartY=-0.5 StartZ=0 EndX=31.4 EndY=-0.5 EndZ=0
    g6: LineSegment StartX=33.4 StartY=-2.5 StartZ=0 EndX=33.4 EndY=-43.5 EndZ=0
    g7: LineSegment StartX=31.4 StartY=-45.5 StartZ=0 EndX=2.40002 EndY=-45.5 EndZ=0
  constraints (17):
    c: Coincident(g7,g3)
    c: Vertical(g6)
    c: Horizontal(g5)
    c: Vertical(g4)
    c: Horizontal(g7)
    c: DistanceX(g-6,g3) = 1
    c: Coincident(g3,g-6)
    c: Coincident(g0,g-5)
    c: Coincident(g1,g-4)
    c: Coincident(g2,g-3)
    c: Tangent(g4,g3) = -1.5708
    c: Tangent(g4,g0) = -1.5708
    c: Tangent(g5,g0) = 1.5708
    c: Tangent(g5,g1) = 1.5708
    c: Tangent(g6,g1) = 1.5708
    c: Tangent(g6,g2) = 1.5708
    c: Tangent(g7,g2) = 1.5708
FEATURE [PartDesign::Pocket] Pocket006
  BaseFeature = -> Fillet004
  Direction = (0,-7e-16,1)
  Length = 3
  Length2 = 5
  Placement = pos=(0,-2.9e-15,6.5) rot=(0,0,1;0rad)
  Profile = -> Sketch010
  ReferenceAxis = -> Sketch010 [N_Axis]
  Type = 0
FEATURE [Sketcher::SketchObject] Sketch011
  ExternalGeometry = -> [Fillet003]
  FullyConstrained = true
  MapMode = 5
  Placement = pos=(0,-1.5,-1.5) rot=(0,0.707107,-0.707107;3.14159rad)
  Support = -> [Fillet003]
  sketch-geometry (8):
    g0: LineSegment StartX=-32.4 StartY=-8 StartZ=0 EndX=-28.9 EndY=-8 EndZ=0
    g1: LineSegment StartX=-28.9 StartY=-8 StartZ=0 EndX=-28.9 EndY=1 EndZ=0
    g2: LineSegment StartX=-28.9 StartY=1 StartZ=0 EndX=-32.4 EndY=1 EndZ=0
    g3: LineSegment StartX=-32.4 StartY=1 StartZ=0 EndX=-32.4 EndY=-8 EndZ=0
    g4: LineSegment StartX=-1.4 StartY=-8 StartZ=0 EndX=-4.9 EndY=-8 EndZ=0
    g5: LineSegment StartX=-4.9 StartY=-8 StartZ=0 EndX=-4.9 EndY=1 EndZ=0
    g6: LineSegment StartX=-4.9 StartY=1 StartZ=0 EndX=-1.4 EndY=1 EndZ=0
    g7: LineSegment StartX=-1.4 StartY=1 StartZ=0 EndX=-1.4 EndY=-8 EndZ=0
  constraints (22):
    c: Coincident(g0,g1)
    c: Coincident(g1,g2)
    c: Coincident(g2,g3)
    c: Coincident(g3,g0)
    c: Horizontal(g0)
    c: Horizontal(g2)
    c: Vertical(g1)
    c: Vertical(g3)
    c: Coincident(g0,g-3)
    c: PointOnObject(g1,g-5)
    c: Coincident(g4,g5)
    c: Coincident(g5,g6)
    c: Coincident(g6,g7)
    c: Coincident(g7,g4)
    c: Horizontal(g4)
    c: Horizontal(g6)
    c: Vertical(g5)
    c: Vertical(g7)
    c: Coincident(g4,g-4)
    c: PointOnObject(g5,g-5)
    c: DistanceX(g2,g2) = 3.5
    c: Equal(g6,g2)
FEATURE [PartDesign::Pad] Pad005
  BaseFeature = -> Fillet003
  Direction = (0,-1,-4e-16)
  Length = 5
  Length2 = 10
  Placement = pos=(0,0,-1.5) rot=(1,0,0;3.14159rad)
  Profile = -> Sketch011
  ReferenceAxis = -> Sketch011 [N_Axis]
  Type = 0
FEATURE [PartDesign::Pad] Pad006
  BaseFeature = -> Pad005
  Direction = (0,1,6e-16)
  Length = 3
  Length2 = 10
  Placement = pos=(0,0,-1.5) rot=(1,0,0;3.14159rad)
  Profile = -> Pad005 [Face18]
  Type = 0
FEATURE [PartDesign::Pad] Pad007
  BaseFeature = -> Pad006
  Direction = (0,1,7e-16)
  Length = 3
  Length2 = 10
  Placement = pos=(0,0,-1.5) rot=(1,0,0;3.14159rad)
  Profile = -> Pad006 [Face21]
  Type = 0
FEATURE [PartDesign::Fillet] Fillet005
  Base = -> Pad007 [Edge78,Edge70,Edge166,Edge161]
  BaseFeature = -> Pad007
  Placement = pos=(0,0,-1.5) rot=(1,0,0;3.14159rad)
  Radius = 3
  SupportTransform = false
  UseAllEdges = false
FEATURE [Sketcher::SketchObject] Sketch012
  ExternalGeometry = -> [Fillet005]
  FullyConstrained = true
  MapMode = 5
  Placement = pos=(0,47.5,-1.5) rot=(-1,0,0;1.5708rad)
  Support = -> [Fillet005]
  sketch-geometry (8):
    g0: LineSegment StartX=1.4 StartY=-8 StartZ=0 EndX=4.9 EndY=-8 EndZ=0
    g1: LineSegment StartX=4.9 StartY=-8 StartZ=0 EndX=4.9 EndY=1 EndZ=0
    g2: LineSegment StartX=4.9 StartY=1 StartZ=0 EndX=1.4 EndY=1 EndZ=0
    g3: LineSegment StartX=1.4 StartY=1 StartZ=0 EndX=1.4 EndY=-8 EndZ=0
    g4: LineSegment StartX=32.4 StartY=-8 StartZ=0 EndX=28.9 EndY=-8 EndZ=0
    g5: LineSegment StartX=28.9 StartY=-8 StartZ=0 EndX=28.9 EndY=1 EndZ=0
    g6: LineSegment StartX=28.9 StartY=1 StartZ=0 EndX=32.4 EndY=1 EndZ=0
    g7: LineSegment StartX=32.4 StartY=1 StartZ=0 EndX=32.4 EndY=-8 EndZ=0
  constraints (22):
    c: Coincident(g0,g1)
    c: Coincident(g1,g2)
    c: Coincident(g2,g3)
    c: Coincident(g3,g0)
    c: Horizontal(g0)
    c: Horizontal(g2)
    c: Vertical(g1)
    c: Vertical(g3)
    c: Coincident(g0,g-4)
    c: PointOnObject(g1,g-3)
    c: Coincident(g4,g5)
    c: Coincident(g5,g6)
    c: Coincident(g6,g7)
    c: Coincident(g7,g4)
    c: Horizontal(g4)
    c: Horizontal(g6)
    c: Vertical(g5)
    c: Vertical(g7)
    c: Coincident(g4,g-5)
    c: PointOnObject(g5,g-3)
    c: DistanceX(g2,g2) = 3.5
    c: Equal(g6,g2)
FEATURE [PartDesign::Pad] Pad008
  BaseFeature = -> Fillet005
  Direction = (0,1,7e-16)
  Length = 5
  Length2 = 10
  Placement = pos=(0,0,-1.5) rot=(1,0,0;3.14159rad)
  Profile = -> Sketch012
  ReferenceAxis = -> Sketch012 [N_Axis]
  Type = 0
FEATURE [PartDesign::Pad] Pad009
  BaseFeature = -> Pad008
  Direction = (0,-1,-9e-16)
  Length = 3
  Length2 = 10
  Placement = pos=(0,0,-1.5) rot=(1,0,0;3.14159rad)
  Profile = -> Pad008 [Face68,Face67]
  Type = 0
FEATURE [PartDesign::Fillet] Fillet006
  Base = -> Pad009 [Edge247,Edge241,Edge143,Edge148]
  BaseFeature = -> Pad009
  Placement = pos=(0,0,-1.5) rot=(1,0,0;3.14159rad)
  Radius = 3
  SupportTransform = false
  UseAllEdges = false
FEATURE [PartDesign::Fillet] Fillet007
  Base = -> Fillet006 [Edge234,Edge247,Edge246,Edge244,Edge242,Edge213,Edge218,Edge217,Edge215,Edge226,Edge221,Edge225,Edge223,Edge239,Edge238,Edge236,Edge230,Edge228,Edge231,Edge229]
  BaseFeature = -> Fillet006
  Placement = pos=(0,0,-1.5) rot=(1,0,0;3.14159rad)
  Radius = 0.8
  SupportTransform = false
  UseAllEdges = false
FEATURE [Sketcher::SketchObject] Sketch014
  ExternalGeometry = -> [Fillet007]
  FullyConstrained = true
  MapMode = 5
  Placement = pos=(32.4,0,-1.5) rot=(0.57735,-0.57735,0.57735;4.18879rad)
  Support = -> [Fillet007]
  sketch-geometry (2):
    g0: Circle CenterX=4 CenterY=-3.5 CenterZ=0 NormalX=0 NormalY=0 NormalZ=1 AngleXU=0 Radius=0.6
    g1: Circle CenterX=-50 CenterY=-3.5 CenterZ=0 NormalX=0 NormalY=0 NormalZ=1 AngleXU=0 Radius=0.6
  constraints (6):
    c: Diameter(g0) = 1.2
    c: Equal(g1,g0)
    c: DistanceY(g0,g-3) = 1.5
    c: DistanceX(g0,g-3) = 2.5
    c: DistanceY(g1,g-4) = 1.5
    c: DistanceX(g-4,g1) = 2.5
FEATURE [PartDesign::Pocket] Pocket007
  BaseFeature = -> Fillet007
  Direction = (-1,0,0)
  Length = 5
  Length2 = 5
  Placement = pos=(0,0,-1.5) rot=(1,0,0;3.14159rad)
  Profile = -> Sketch014
  ReferenceAxis = -> Sketch014 [N_Axis]
  Type = 1
FEATURE [PartDesign::Pad] Pad010
  BaseFeature = -> Pocket007
  Direction = (0,-1.4e-15,1)
  Length = 1
  Length2 = 10
  Placement = pos=(0,0,-1.5) rot=(1,0,0;3.14159rad)
  Profile = -> Pocket007 [Face64]
  Type = 0
FEATURE [Sketcher::SketchObject] Sketch015
  ExternalGeometry = -> [Pad010]
  FullyConstrained = true
  MapMode = 5
  Placement = pos=(0,-1e-15,0.5) rot=(0,0,1;0rad)
  sketch-geometry (4):
    g0: LineSegment StartX=0.48 StartY=9.57 StartZ=0 EndX=33.31 EndY=9.57 EndZ=0
    g1: LineSegment StartX=33.31 StartY=9.57 StartZ=0 EndX=33.31 EndY=3.87 EndZ=0
    g2: LineSegment StartX=33.31 StartY=3.87 StartZ=0 EndX=0.48 EndY=3.87 EndZ=0
    g3: LineSegment StartX=0.48 StartY=3.87 StartZ=0 EndX=0.48 EndY=9.57 EndZ=0
  constraints (10):
    c: Coincident(g0,g1)
    c: Coincident(g1,g2)
    c: Coincident(g2,g3)
    c: Coincident(g3,g0)
    c: Horizontal(g2)
    c: Vertical(g1)
    c: Vertical(g3)
    c: Coincident(g0,g-3)
    c: DistanceY(g3,g3) = 5.7
    c: Coincident(g0,g-3)
FEATURE [PartDesign::Pocket] Pocket008
  BaseFeature = -> Pad010
  Direction = (0,0,-1)
  Length = 1.52
  Length2 = 5
  Placement = pos=(0,0,-1.5) rot=(1,0,0;3.14159rad)
  Profile = -> Sketch015
  ReferenceAxis = -> Sketch015 [N_Axis]
  Type = 0
FEATURE [PartDesign::ShapeBinder] ShapeBinder
  Support = -> [Part__Feature055]
  TraceSupport = false
FEATURE [Sketcher::SketchObject] Sketch016
  ExternalGeometry = -> [ShapeBinder]
  FullyConstrained = true
  MapMode = 5
  Placement = pos=(0,-1e-15,0.5) rot=(0,0,1;0rad)
  sketch-geometry (8):
    g0: ArcOfCircle CenterX=3.9 CenterY=42.96 CenterZ=0 NormalX=0 NormalY=0 NormalZ=1 AngleXU=0 Radius=0.8 StartAngle=1.5708 EndAngle=4.71239
    g1: ArcOfCircle CenterX=29.9 CenterY=42.96 CenterZ=0 NormalX=0 NormalY=0 NormalZ=1 AngleXU=0 Radius=0.8 StartAngle=4.71239 EndAngle=7.85398
    g2: LineSegment StartX=3.9 StartY=43.76 StartZ=0 EndX=29.9 EndY=43.76 EndZ=0
    g3: LineSegment StartX=29.9 StartY=42.16 StartZ=0 EndX=3.9 EndY=42.16 EndZ=0
    g4: ArcOfCircle CenterX=3.9 CenterY=3 CenterZ=0 NormalX=0 NormalY=0 NormalZ=1 AngleXU=0 Radius=0.8 StartAngle=1.5708 EndAngle=4.71239
    g5: ArcOfCircle CenterX=29.9 CenterY=3 CenterZ=0 NormalX=0 NormalY=0 NormalZ=1 AngleXU=0 Radius=0.8 StartAngle=4.71239 EndAngle=7.85398
    g6: LineSegment StartX=3.9 StartY=3.8 StartZ=0 EndX=29.9 EndY=3.8 EndZ=0
    g7: LineSegment StartX=29.9 StartY=2.2 StartZ=0 EndX=3.9 EndY=2.2 EndZ=0
  constraints (18):
    c: Coincident(g0,g-5)
    c: Diameter(g0) = 1.6
    c: Coincident(g1,g-6)
    c: Equal(g0,g1)
    c: Coincident(g2,g1)
    c: Horizontal(g2)
    c: Coincident(g3,g1)
    c: Horizontal(g3)
    c: Tangent(g3,g0) = 1.5708
    c: Tangent(g2,g0) = 1.5708
    c: Coincident(g4,g-8)
    c: Coincident(g5,g-10)
    c: Equal(g4,g5)
    c: Tangent(g7,g4) = 1.5708
    c: Tangent(g6,g4) = 1.5708
    c: Tangent(g6,g5) = 1.5708
    c: Tangent(g7,g5) = 1.5708
    c: Equal(g4,g0)
FEATURE [PartDesign::Pad] Pad011
  BaseFeature = -> Pocket008
  Direction = (0,-1e-15,1)
  Length = 4
  Length2 = 10
  Placement = pos=(0,0,-1.5) rot=(1,0,0;3.14159rad)
  Profile = -> Sketch016
  ReferenceAxis = -> Sketch016 [N_Axis]
  Type = 0
FEATURE [PartDesign::ShapeBinder] ShapeBinder001
  Support = -> [Pad011]
  TraceSupport = false
FEATURE [Sketcher::SketchObject] Sketch020
  FullyConstrained = false
  MapMode = 5
  Placement = pos=(0,-1.2e-14,4.5) rot=(0,0,1;0rad)
  sketch-geometry (6):
    g0: Circle CenterX=5.9 CenterY=42.96 CenterZ=0 NormalX=0 NormalY=0 NormalZ=1 AngleXU=0 Radius=0.9
    g1: Circle CenterX=27.9 CenterY=42.96 CenterZ=0 NormalX=0 NormalY=0 NormalZ=1 AngleXU=0 Radius=0.9
    g2: Circle CenterX=5.9 CenterY=3 CenterZ=0 NormalX=0 NormalY=0 NormalZ=1 AngleXU=0 Radius=0.9
    g3: Circle CenterX=27.9 CenterY=3 CenterZ=0 NormalX=0 NormalY=0 NormalZ=1 AngleXU=0 Radius=0.9
    g4: LineSegment StartX=3.9 StartY=3 StartZ=0 EndX=29.9 EndY=3 EndZ=0
    g5: LineSegment StartX=3.9 StartY=42.96 StartZ=0 EndX=29.9 EndY=42.96 EndZ=0
  constraints (12):
    c: PointOnObject(g1,g5)
    c: PointOnObject(g0,g5)
    c: PointOnObject(g2,g4)
    c: PointOnObject(g3,g4)
    c: DistanceX(g5,g0) = 2
    c: DistanceX(g1,g5) = 2
    c: DistanceX(g4,g2) = 2
    c: DistanceX(g3,g4) = 2
    c: Diameter(g0) = 1.8
    c: Equal(g0,g1)
    c: Equal(g1,g3)
    c: Equal(g3,g2)
FEATURE [PartDesign::Pocket] Pocket011
  BaseFeature = -> Pad011
  Direction = (0,2e-15,-1)
  Length = 3
  Length2 = 5
  Placement = pos=(0,0,-1.5) rot=(1,0,0;3.14159rad)
  Profile = -> Sketch020
  ReferenceAxis = -> Sketch020 [N_Axis]
  Type = 0
FEATURE [Sketcher::SketchObject] Sketch021
  FullyConstrained = false
  MapMode = 5
  Placement = pos=(0,-8e-15,6.5) rot=(1,0,0;3.14159rad)
  sketch-geometry (16):
    g0: ArcOfCircle CenterX=2.4 CenterY=-2.5 CenterZ=0 NormalX=0 NormalY=0 NormalZ=1 AngleXU=0 Radius=2.65 StartAngle=1.5708 EndAngle=3.1416
    g1: LineSegment StartX=2.4 StartY=0.15 StartZ=0 EndX=31.4 EndY=0.15 EndZ=0
    g2: ArcOfCircle CenterX=31.4 CenterY=-2.5 CenterZ=0 NormalX=0 NormalY=0 NormalZ=1 AngleXU=0 Radius=2.65 StartAngle=0 EndAngle=1.5708
    g3: LineSegment StartX=34.05 StartY=-2.5 StartZ=0 EndX=34.05 EndY=-43.5 EndZ=0
    g4: ArcOfCircle CenterX=31.4 CenterY=-43.5 CenterZ=0 NormalX=0 NormalY=0 NormalZ=1 AngleXU=0 Radius=2.65 StartAngle=4.71239 EndAngle=6.28319
    g5: LineSegment StartX=31.4 StartY=-46.15 StartZ=0 EndX=2.4 EndY=-46.15 EndZ=0
    g6: ArcOfCircle CenterX=2.4 CenterY=-43.5 CenterZ=0 NormalX=0 NormalY=0 NormalZ=1 AngleXU=0 Radius=2.65 StartAngle=3.14159 EndAngle=4.71239
    g7: LineSegment StartX=-0.25 StartY=-43.5 StartZ=0 EndX=-0.25 EndY=-2.50001 EndZ=0
    g8: ArcOfCircle CenterX=2.4 CenterY=-2.5 CenterZ=0 NormalX=0 NormalY=0 NormalZ=1 AngleXU=0 Radius=2 StartAngle=1.5708 EndAngle=3.14159
    g9: ArcOfCircle CenterX=31.4 CenterY=-2.5 CenterZ=0 NormalX=0 NormalY=0 NormalZ=1 AngleXU=0 Radius=2 StartAngle=0 EndAngle=1.5708
    g10: ArcOfCircle CenterX=31.4 CenterY=-43.5 CenterZ=0 NormalX=0 NormalY=0 NormalZ=1 AngleXU=0 Radius=2 StartAngle=4.71239 EndAngle=6.28319
    g11: ArcOfCircle CenterX=2.4 CenterY=-43.5 CenterZ=0 NormalX=0 NormalY=0 NormalZ=1 AngleXU=0 Radius=2 StartAngle=3.14159 EndAngle=4.71239
    g12: LineSegment StartX=2.4 StartY=-0.5 StartZ=0 EndX=31.4 EndY=-0.5 EndZ=0
    g13: LineSegment StartX=33.4 StartY=-2.5 StartZ=0 EndX=33.4 EndY=-43.5 EndZ=0
    g14: LineSegment StartX=31.4 StartY=-45.5 StartZ=0 EndX=2.4 EndY=-45.5 EndZ=0
    g15: LineSegment StartX=0.4 StartY=-43.5 StartZ=0 EndX=0.4 EndY=-2.5 EndZ=0
  constraints (27):
    c: Vertical(g3)
    c: Horizontal(g5)
    c: Coincident(g7,g0)
    c: Vertical(g7)
    c: Tangent(g1,g0) = 1.5708
    c: Tangent(g2,g1) = 1.5708
    c: Tangent(g3,g2) = 1.5708
    c: Tangent(g4,g3) = 1.5708
    c: Tangent(g5,g4) = 1.5708
    c: Tangent(g6,g5) = 1.5708
    c: Tangent(g7,g6) = 1.5708
    c: Coincident(g8,g0)
    c: Coincident(g9,g2)
    c: Coincident(g10,g4)
    c: Coincident(g11,g6)
    c: Coincident(g12,g8)
    c: Coincident(g12,g9)
    c: Horizontal(g12)
    c: Vertical(g13)
    c: Horizontal(g14)
    c: Vertical(g15)
    c: Tangent(g15,g8) = 1.5708
    c: Tangent(g15,g11) = 1.5708
    c: Tangent(g14,g11) = 1.5708
    c: Tangent(g14,g10) = 1.5708
    c: Tangent(g13,g10) = 1.5708
    c: Tangent(g13,g9) = 1.5708
FEATURE [PartDesign::Pad] Pad013
  BaseFeature = -> Pocket006
  Direction = (0,4e-15,-1)
  Length = 1
  Length2 = 10
  Placement = pos=(0,-2.9e-15,6.5) rot=(0,0,1;0rad)
  Profile = -> Sketch021
  ReferenceAxis = -> Sketch021 [N_Axis]
  Type = 0
FEATURE [Sketcher::SketchObject] Sketch022
  ExternalGeometry = -> [Pad013]
  FullyConstrained = true
  MapMode = 5
  Placement = pos=(0,-5.1e-15,9.5) rot=(1,0,0;3.14159rad)
  Support = -> [Pad013]
  sketch-geometry (9):
    g0: GeomPoint X=16.9 Y=-23 Z=0
    g1: LineSegment StartX=2.9 StartY=-10 StartZ=0 EndX=30.9 EndY=-10 EndZ=0
    g2: LineSegment StartX=30.9 StartY=-10 StartZ=0 EndX=30.9 EndY=-13 EndZ=0
    g3: LineSegment StartX=30.9 StartY=-13 StartZ=0 EndX=2.9 EndY=-13 EndZ=0
    g4: LineSegment StartX=2.9 StartY=-13 StartZ=0 EndX=2.9 EndY=-10 EndZ=0
    g5: LineSegment StartX=2.9 StartY=-33 StartZ=0 EndX=30.9 EndY=-33 EndZ=0
    g6: LineSegment StartX=30.9 StartY=-33 StartZ=0 EndX=30.9 EndY=-36 EndZ=0
    g7: LineSegment StartX=30.9 StartY=-36 StartZ=0 EndX=2.9 EndY=-36 EndZ=0
    g8: LineSegment StartX=2.9 StartY=-36 StartZ=0 EndX=2.9 EndY=-33 EndZ=0
  constraints (23):
    c: Coincident(g1,g2)
    c: Coincident(g2,g3)
    c: Coincident(g3,g4)
    c: Coincident(g4,g1)
    c: Horizontal(g1)
    c: Horizontal(g3)
    c: Vertical(g2)
    c: Vertical(g4)
    c: Coincident(g5,g6)
    c: Coincident(g6,g7)
    c: Coincident(g7,g8)
    c: Coincident(g8,g5)
    c: Horizontal(g7)
    c: Vertical(g6)
    c: Vertical(g8)
    c: DistanceX(g1,g1) = 28
    c: DistanceY(g2,g2) = 3
    c: Equal(g2,g6)
    c: Symmetric(g5,g2,g0)
    c: Symmetric(g5,g3,g0)
    c: DistanceX(g5,g3) = 0
    c: DistanceY(g5,g2) = 20
    c: Symmetric(g-3,g-4,g0)
FEATURE [PartDesign::Pad] Pad014
  BaseFeature = -> Pad013
  Direction = (0,1.5e-15,-1)
  Length = 3
  Length2 = 10
  Placement = pos=(0,-2.9e-15,6.5) rot=(0,0,1;0rad)
  Profile = -> Sketch022
  ReferenceAxis = -> Sketch022 [N_Axis]
  Type = 0
FEATURE [Sketcher::SketchObject] Sketch023
  ExternalGeometry = -> [Pad014]
  FullyConstrained = true
  MapMode = 5
  Placement = pos=(0,-5.1e-15,9.5) rot=(1,0,0;3.14159rad)
  Support = -> [Pad014]
  sketch-geometry (12):
    g0: ArcOfCircle CenterX=2.4 CenterY=-43.5 CenterZ=0 NormalX=0 NormalY=0 NormalZ=1 AngleXU=0 Radius=2 StartAngle=3.14159 EndAngle=4.71239
    g1: ArcOfCircle CenterX=31.4 CenterY=-43.5 CenterZ=0 NormalX=0 NormalY=0 NormalZ=1 AngleXU=0 Radius=2 StartAngle=4.71239 EndAngle=6.28319
    g2: ArcOfCircle CenterX=2.4 CenterY=-2.5 CenterZ=0 NormalX=0 NormalY=0 NormalZ=1 AngleXU=0 Radius=2 StartAngle=1.5708 EndAngle=3.14159
    g3: ArcOfCircle CenterX=31.4 CenterY=-2.5 CenterZ=0 NormalX=0 NormalY=0 NormalZ=1 AngleXU=0 Radius=2 StartAngle=0 EndAngle=1.5708
    g4: LineSegment StartX=2.4 StartY=-0.5 StartZ=0 EndX=31.4 EndY=-0.5 EndZ=0
    g5: LineSegment StartX=2.4 StartY=-45.5 StartZ=0 EndX=31.4 EndY=-45.5 EndZ=0
    g6: LineSegment StartX=0.4 StartY=-43.5 StartZ=0 EndX=0.4 EndY=-39.7 EndZ=0
    g7: LineSegment StartX=0.4 StartY=-39.7 StartZ=0 EndX=33.4 EndY=-39.7 EndZ=0
    g8: LineSegment StartX=33.4 StartY=-39.7 StartZ=0 EndX=33.4 EndY=-43.5 EndZ=0
    g9: LineSegment StartX=0.4 StartY=-2.5 StartZ=0 EndX=0.4 EndY=-6.3 EndZ=0
    g10: LineSegment StartX=0.4 StartY=-6.3 StartZ=0 EndX=33.4 EndY=-6.3 EndZ=0
    g11: LineSegment StartX=33.4 StartY=-6.3 StartZ=0 EndX=33.4 EndY=-2.5 EndZ=0
  constraints (32):
    c: Coincident(g0,g-6)
    c: Coincident(g0,g-6)
    c: Coincident(g0,g-7)
    c: Coincident(g1,g-8)
    c: Coincident(g1,g-8)
    c: Coincident(g1,g-8)
    c: Coincident(g2,g-5)
    c: Coincident(g2,g-5)
    c: Coincident(g2,g-5)
    c: Coincident(g3,g-3)
    c: Coincident(g3,g-4)
    c: Coincident(g3,g-3)
    c: Coincident(g4,g2)
    c: Coincident(g4,g3)
    c: Coincident(g5,g0)
    c: Coincident(g5,g1)
    c: Coincident(g6,g0)
    c: Vertical(g6)
    c: Coincident(g7,g6)
    c: Horizontal(g7)
    c: Coincident(g8,g7)
    c: Coincident(g8,g1)
    c: Vertical(g8)
    c: DistanceY(g8,g8) = 3.8
    c: Coincident(g9,g2)
    c: Vertical(g9)
    c: Coincident(g10,g9)
    c: Horizontal(g10)
    c: Coincident(g11,g10)
    c: Coincident(g11,g3)
    c: Vertical(g11)
    c: Equal(g11,g8)
FEATURE [PartDesign::Pad] Pad015
  BaseFeature = -> Pad014
  Direction = (0,1.8e-15,-1)
  Length = 4
  Length2 = 10
  Placement = pos=(0,-2.9e-15,6.5) rot=(0,0,1;0rad)
  Profile = -> Sketch023
  ReferenceAxis = -> Sketch023 [N_Axis]
  Type = 0
FEATURE [Sketcher::SketchObject] Sketch024
  ExternalGeometry = -> [ShapeBinder001]
  FullyConstrained = true
  MapMode = 5
  Placement = pos=(0,-1.1e-15,5.5) rot=(1,0,0;3.14159rad)
  Support = -> [Pad015]
  sketch-geometry (6):
    g0: Circle CenterX=5.9 CenterY=-42.96 CenterZ=0 NormalX=0 NormalY=0 NormalZ=1 AngleXU=0 Radius=1
    g1: Circle CenterX=27.9 CenterY=-42.96 CenterZ=0 NormalX=0 NormalY=0 NormalZ=1 AngleXU=0 Radius=1
    g2: Circle CenterX=5.9 CenterY=-3 CenterZ=0 NormalX=0 NormalY=0 NormalZ=1 AngleXU=0 Radius=1
    g3: Circle CenterX=27.9 CenterY=-3 CenterZ=0 NormalX=0 NormalY=0 NormalZ=1 AngleXU=0 Radius=1
    g4: LineSegment StartX=3.9 StartY=-42.96 StartZ=0 EndX=29.9 EndY=-42.96 EndZ=0
    g5: LineSegment StartX=3.9 StartY=-3 StartZ=0 EndX=29.9 EndY=-3 EndZ=0
  constraints (16):
    c: PointOnObject(g3,g5)
    c: PointOnObject(g2,g5)
    c: PointOnObject(g0,g4)
    c: PointOnObject(g1,g4)
    c: Diameter(g0) = 2
    c: Equal(g1,g0)
    c: Equal(g0,g2)
    c: Equal(g2,g3)
    c: DistanceX(g5,g2) = 2
    c: DistanceX(g3,g5) = 2
    c: DistanceX(g4,g0) = 2
    c: DistanceX(g1,g4) = 2
    c: Coincident(g5,g-3)
    c: Coincident(g5,g-4)
    c: Coincident(g4,g-5)
    c: Coincident(g4,g-6)
FEATURE [PartDesign::Pocket] Pocket012
  BaseFeature = -> Pad015
  Direction = (0,-2.2e-15,1)
  Length = 5
  Length2 = 5
  Placement = pos=(0,-2.9e-15,6.5) rot=(0,0,1;0rad)
  Profile = -> Sketch024
  ReferenceAxis = -> Sketch024 [N_Axis]
  Type = 1
FEATURE [Sketcher::SketchObject] Sketch025
  ExternalGeometry = -> [Pocket012]
  FullyConstrained = true
  MapMode = 5
  Placement = pos=(0,-4.3e-15,10.5) rot=(0,0,1;0rad)
  Support = -> [Pocket012]
  sketch-geometry (4):
    g0: Circle CenterX=5.9 CenterY=42.96 CenterZ=0 NormalX=0 NormalY=0 NormalZ=1 AngleXU=0 Radius=2.125
    g1: Circle CenterX=27.9 CenterY=42.96 CenterZ=0 NormalX=0 NormalY=0 NormalZ=1 AngleXU=0 Radius=2.125
    g2: Circle CenterX=5.9 CenterY=3 CenterZ=0 NormalX=0 NormalY=0 NormalZ=1 AngleXU=0 Radius=2.125
    g3: Circle CenterX=27.9 CenterY=3 CenterZ=0 NormalX=0 NormalY=0 NormalZ=1 AngleXU=0 Radius=2.125
  constraints (8):
    c: Coincident(g0,g-3)
    c: Coincident(g1,g-4)
    c: Coincident(g2,g-5)
    c: Coincident(g3,g-6)
    c: Diameter(g0) = 4.25
    c: Equal(g0,g1)
    c: Equal(g1,g3)
    c: Equal(g3,g2)
FEATURE [PartDesign::Pocket] Pocket013
  BaseFeature = -> Pocket012
  Direction = (0,2.6e-15,-1)
  Length = 3
  Length2 = 5
  Placement = pos=(0,-2.9e-15,6.5) rot=(0,0,1;0rad)
  Profile = -> Sketch025
  ReferenceAxis = -> Sketch025 [N_Axis]
  Type = 0
FEATURE [PartDesign::Fillet] Fillet009
  Base = -> Pocket013 [Edge136,Edge132,Edge131,Edge134,Edge139,Edge142,Edge140,Edge144]
  BaseFeature = -> Pocket013
  Placement = pos=(0,-2.9e-15,6.5) rot=(0,0,1;0rad)
  Radius = 1
  SupportTransform = false
  UseAllEdges = false
FEATURE [PartDesign::Body] Body002  label="Case_Bottom"
  Group = -> [DatumPlane001,ReferenceFillet003,Sketch009,Pad004,Fillet004,Sketch010,Pocket006,ShapeBinder001,Sketch021,Pad013,Sketch022,Pad014,Sketch023,Pad015,Sketch024,Pocket012,Sketch025,Pocket013,Fillet009]
  Origin = -> Origin115
  Tip = -> Fillet009
FEATURE [PartDesign::Pad] Pad016
  BaseFeature = -> Pocket011
  Direction = (0,-1.8e-15,1)
  Length = 0.4
  Length2 = 10
  Placement = pos=(0,0,-1.5) rot=(1,0,0;3.14159rad)
  Profile = -> Pocket011 [Face66]
  Type = 0
FEATURE [PartDesign::Pad] Pad018
  BaseFeature = -> Pad016
  Direction = (0,-1.4e-15,1)
  Length = 0.5
  Length2 = 10
  Placement = pos=(0,0,-1.5) rot=(1,0,0;3.14159rad)
  Profile = -> Pad016 [Face169,Face173,Face177,Face180,Face184,Face188]
  Type = 0
FEATURE [Part::Part2DObjectPython] ShapeString  # Draft 2D object (typed FeaturePython)
  FontFile = <userpath>/Téléchargements/ubuntu/Ubuntu-B.ttf
  MakeFace = true
  Placement = pos=(28.3629,3.34221,-2.5) rot=(0,1,0;3.14159rad)
  Size = 2.5
  String = Watchy
  Tracking = 0
FEATURE [Part::Extrusion] Extrude  label="Watchy"
  Base = -> ShapeString
  Dir = (0,0,-1)
  DirMode = 2
  FaceMakerClass = Part::FaceMakerBullseye
  LengthFwd = 0.5
  LengthRev = 0
  Placement = pos=(0.184744,0.772381,0.5) rot=(0,0,1;0rad)
  Solid = false
  Symmetric = false
FEATURE [PartDesign::ShapeBinder] ReferencePart__Feature055
  Support = -> [Part__Feature055]
  TraceSupport = false
FEATURE [PartDesign::Plane] DatumPlane002
  Length = 70.0989
  MapMode = 5
  Placement = pos=(0,0,1.6) rot=(0,0,1;0rad)
  ResizeMode = 0
  Support = -> [ReferencePart__Feature055]
  Width = 83.1771
FEATURE [Sketcher::SketchObject] Sketch026
  ExternalGeometry = -> [ReferencePart__Feature055]
  FullyConstrained = true
  MapMode = 5
  Placement = pos=(0,0,1.6) rot=(0,0,1;0rad)
  Support = -> [DatumPlane002]
  sketch-geometry (8):
    g0: ArcOfCircle CenterX=3.9 CenterY=42.96 CenterZ=0 NormalX=0 NormalY=0 NormalZ=1 AngleXU=0 Radius=1 StartAngle=1.5708 EndAngle=4.71239
    g1: ArcOfCircle CenterX=29.9 CenterY=42.96 CenterZ=0 NormalX=0 NormalY=0 NormalZ=1 AngleXU=0 Radius=1 StartAngle=4.71239 EndAngle=7.85398
    g2: LineSegment StartX=3.9 StartY=43.96 StartZ=0 EndX=29.9 EndY=43.96 EndZ=0
    g3: LineSegment StartX=29.9 StartY=41.96 StartZ=0 EndX=3.9 EndY=41.96 EndZ=0
    g4: ArcOfCircle CenterX=3.9 CenterY=42.96 CenterZ=0 NormalX=0 NormalY=0 NormalZ=1 AngleXU=0 Radius=2.5 StartAngle=1.5708 EndAngle=4.71239
    g5: ArcOfCircle CenterX=29.9 CenterY=42.96 CenterZ=0 NormalX=0 NormalY=0 NormalZ=1 AngleXU=0 Radius=2.5 StartAngle=4.71239 EndAngle=7.85398
    g6: LineSegment StartX=3.9 StartY=45.46 StartZ=0 EndX=29.9 EndY=45.46 EndZ=0
    g7: LineSegment StartX=3.9 StartY=40.46 StartZ=0 EndX=29.9 EndY=40.46 EndZ=0
  constraints (19):
    c: Coincident(g0,g-4)
    c: Coincident(g0,g-4)
    c: Coincident(g0,g-5)
    c: Coincident(g1,g-6)
    c: Coincident(g1,g-6)
    c: Coincident(g1,g-6)
    c: Coincident(g2,g0)
    c: Coincident(g2,g1)
    c: Coincident(g3,g1)
    c: Coincident(g3,g0)
    c: Coincident(g5,g1)
    c: Horizontal(g6)
    c: Horizontal(g7)
    c: DistanceY(g0,g4) = 1.5
    c: Tangent(g6,g4) = 1.5708
    c: Tangent(g6,g5) = 1.5708
    c: Tangent(g7,g5) = -1.5708
    c: Tangent(g7,g4) = -1.5708
    c: Coincident(g0,g4)
FEATURE [PartDesign::Pad] Pad019
  Direction = (0,0,1)
  Length = 3.5
  Length2 = 10
  Placement = pos=(0,0,1.6) rot=(0,0,1;0rad)
  Profile = -> Sketch026
  ReferenceAxis = -> Sketch026 [N_Axis]
  Type = 0
FEATURE [PartDesign::Body] Body003  label="Bride"
  Group = -> [DatumPlane002,ReferencePart__Feature055,Sketch026,Pad019]
  Origin = -> Origin116
  Tip = -> Pad019
FEATURE [PartDesign::FeatureBase] Clone
  BaseFeature = -> Body003
FEATURE [PartDesign::Body] Body004  label="Bride2"
  BaseFeature = -> Body003
  Group = -> [Clone]
  Origin = -> Origin117
  Placement = pos=(0,-40,0) rot=(0,0,1;0rad)
  Tip = -> Clone
FEATURE [Mesh::Feature] Micro_USB_Cover
  Placement = pos=(36.4,26.7,5) rot=(0.707107,-0.707107,0;3.14159rad)
FEATURE [Part::Feature] Micro_USB_Cover001
  shape: bbox 6 x 8.5 x 3.5 mm, 1068 faces, 0 solids (baked)
FEATURE [Sketcher::SketchObject] Sketch027
  FullyConstrained = true
  MapMode = 5
  Placement = pos=(0,0,0) rot=(0.57735,0.57735,0.57735;2.0944rad)
  Support = -> [YZ_Plane118]
  sketch-geometry (4):
    g0: LineSegment StartX=17.7 StartY=5.55 StartZ=0 EndX=27.2 EndY=5.55 EndZ=0
    g1: LineSegment StartX=27.2 StartY=5.55 StartZ=0 EndX=27.2 EndY=0.95 EndZ=0
    g2: LineSegment StartX=27.2 StartY=0.95 StartZ=0 EndX=17.7 EndY=0.95 EndZ=0
    g3: LineSegment StartX=17.7 StartY=0.95 StartZ=0 EndX=17.7 EndY=5.55 EndZ=0
  constraints (12):
    c: Coincident(g0,g1)
    c: Coincident(g1,g2)
    c: Coincident(g2,g3)
    c: Coincident(g3,g0)
    c: Horizontal(g0)
    c: Horizontal(g2)
    c: Vertical(g1)
    c: Vertical(g3)
    c: DistanceX(g0,g0) = 9.5
    c: DistanceY(g1,g1) = 4.6
    c: DistanceY(g-1,g2) = 0.95
    c: DistanceX(g-1,g2) = 17.7
FEATURE [PartDesign::Pad] Pad020
  Direction = (1,-2e-16,3e-16)
  Length = 2
  Length2 = 10
  Placement = pos=(0,0,0) rot=(0.57735,0.57735,0.57735;2.0944rad)
  Profile = -> Sketch027
  ReferenceAxis = -> Sketch027 [N_Axis]
  Type = 0
FEATURE [Part::Feature] Micro_USB_Cover001_solid  label="Micro_USB_Cover001 (Solid)"
  Placement = pos=(0.5,0,0) rot=(0,0,1;0rad)
  shape: bbox 6 x 8.5 x 3.5 mm, 1068 faces (baked)
FEATURE [PartDesign::ShapeBinder] ShapeBinder002
  Support = -> [Micro_USB_Cover001_solid]
  TraceSupport = false
FEATURE [PartDesign::Fillet] Fillet010
  Base = -> Pad020 [Edge1,Edge8,Edge5,Edge2,Edge4,Edge7,Edge10,Edge12]
  BaseFeature = -> Pad020
  Placement = pos=(0,0,0) rot=(0.57735,0.57735,0.57735;2.0944rad)
  Radius = 1
  SupportTransform = false
  UseAllEdges = false
FEATURE [PartDesign::Body] Body005
  Group = -> [Sketch027,Pad020,ShapeBinder002,Fillet010]
  Origin = -> Origin118
  Placement = pos=(35.4,0,0) rot=(0,0,1;0rad)
  Tip = -> Fillet010
FEATURE [Part::Fuse] Fusion  label="USB_Cap"
  Base = -> Body005
  Tool = -> Micro_USB_Cover001_solid
FEATURE [PartDesign::ShapeBinder] ShapeBinder003
  Placement = pos=(0,0,-2.5) rot=(1,0,0;3.14159rad)
  Support = -> [Sketch002]
  TraceSupport = false
FEATURE [Sketcher::SketchObject] Sketch028
  ExternalGeometry = -> [ShapeBinder003]
  FullyConstrained = true
  MapMode = 5
  Placement = pos=(0,0,-1.5) rot=(1,0,0;3.14159rad)
  Support = -> [Pocket]
  sketch-geometry (4):
    g0: LineSegment StartX=3 StartY=-12.3 StartZ=0 EndX=31 EndY=-12.3 EndZ=0
    g1: LineSegment StartX=31 StartY=-39.3 StartZ=0 EndX=31 EndY=-12.3 EndZ=0
    g2: LineSegment StartX=31 StartY=-39.3 StartZ=0 EndX=3 EndY=-39.3 EndZ=0
    g3: LineSegment StartX=3 StartY=-12.3 StartZ=0 EndX=3 EndY=-39.3 EndZ=0
  constraints (8):
    c: Coincident(g0,g-3)
    c: Coincident(g0,g-4)
    c: Coincident(g1,g-5)
    c: Coincident(g1,g0)
    c: Coincident(g2,g1)
    c: Coincident(g2,g-5)
    c: Coincident(g3,g0)
    c: Coincident(g3,g2)
FEATURE [PartDesign::Pad] Pad021
  BaseFeature = -> Pocket
  Direction = (0,0,-1)
  Length = 0.8
  Length2 = 10
  Profile = -> Sketch028
  ReferenceAxis = -> Sketch028 [N_Axis]
  Type = 0
FEATURE [PartDesign::Body] Body  label="Vitre"
  Group = -> [Sketch,Pad,Fillet,Pocket,ShapeBinder003,Sketch028,Pad021]
  Origin = -> Origin056
  Tip = -> Pad021
FEATURE [PartDesign::Pocket] Pocket014
  BaseFeature = -> Pad018
  Direction = (0,2.1e-15,-1)
  Length = 0.73
  Length2 = 5
  Placement = pos=(0,0,-1.5) rot=(1,0,0;3.14159rad)
  Profile = -> Pad018 [Face67]
  Type = 0
FEATURE [PartDesign::Pocket] Pocket015
  BaseFeature = -> Pocket014
  Direction = (0,2e-15,-1)
  Length = 0.33
  Length2 = 5
  Placement = pos=(0,0,-1.5) rot=(1,0,0;3.14159rad)
  Profile = -> Pocket014 [Face113,Face111,Face117,Face116]
  Type = 0
FEATURE [Sketcher::SketchObject] Sketch029
  ExternalGeometry = -> [Pocket015]
  FullyConstrained = true
  MapMode = 5
  Placement = pos=(0,-3e-16,0.65) rot=(0,0,1;0rad)
  Support = -> [Pocket015]
  sketch-geometry (4):
    g0: LineSegment StartX=34.7 StartY=26.9 StartZ=0 EndX=35.1 EndY=26.9 EndZ=0
    g1: LineSegment StartX=35.1 StartY=26.9 StartZ=0 EndX=35.1 EndY=18 EndZ=0
    g2: LineSegment StartX=35.1 StartY=18 StartZ=0 EndX=34.7 EndY=18 EndZ=0
    g3: LineSegment StartX=34.7 StartY=18 StartZ=0 EndX=34.7 EndY=26.9 EndZ=0
  constraints (12):
    c: Coincident(g0,g1)
    c: Coincident(g1,g2)
    c: Coincident(g2,g3)
    c: Coincident(g3,g0)
    c: Horizontal(g0)
    c: Horizontal(g2)
    c: Vertical(g1)
    c: Vertical(g3)
    c: DistanceX(g0,g0) = 0.4
    c: DistanceY(g-4,g0) = 1
    c: DistanceY(g1,g-4) = 1
    c: DistanceX(g-3,g0) = 0.3
FEATURE [PartDesign::Pad] Pad022
  BaseFeature = -> Pocket015
  Direction = (0,-2.2e-15,1)
  Length = 5
  Length2 = 10
  Placement = pos=(0,0,-1.5) rot=(1,0,0;3.14159rad)
  Profile = -> Sketch029
  ReferenceAxis = -> Sketch029 [N_Axis]
  Type = 0
FEATURE [PartDesign::Body] Body001  label="Case_Top"
  Group = -> [DatumPlane,ReferencePocket,Sketch001,Pad001,Sketch002,Pocket001,Sketch003,Pocket002,Sketch004,Pocket003,Sketch005,Pocket004,Sketch006,Pocket005,Sketch007,Pad002,Sketch008,Pad003,Fillet001,Fillet002,Fillet003,Sketch011,Pad005,Pad006,Pad007,Fillet005,Sketch012,Pad008,Pad009,Fillet006,Fillet007,Sketch014,Pocket007,Pad010,Sketch015,Pocket008,Sketch016,ShapeBinder,Pad011,Sketch020,Pocket011,Pad016,+5 more]
  Origin = -> Origin057
  Tip = -> Pad022
FEATURE [Part::Cut] Cut  label="Case_Top_Watchy"
  Base = -> Body001
  Tool = -> Extrude
FEATURE [PartDesign::ShapeBinder] ShapeBinder004
  Placement = pos=(0,0,-0.8) rot=(0,0,1;0rad)
  Support = -> [Pad021]
  TraceSupport = false
FEATURE [PartDesign::ShapeBinder] ShapeBinder005
  Support = -> [Pad021]
  TraceSupport = false
FEATURE [Part::Feature] Part__Feature056  label="SOLID010"
  shape: bbox 4 x 4 x 1.1 mm, 158 faces (baked)
FEATURE [App::Part] QFN_24_1EP_4x4mm_P0_5mm_EP2_7x2_7mm001  label="QFN-24-1EP_4x4mm_P0.5mm_EP2.7x2.7mm001"
  Group = -> [Part__Feature056]
  Origin = -> Origin135
  Placement = pos=(25.76,24.38,1.05) rot=(0,0,1;0rad)
FEATURE [Part::Feature] Part__Feature057  label="SOLID011"
  shape: bbox 3.8 x 1.6 x 1.25 mm, 67 faces (baked)
FEATURE [App::Part] D_SOD_123004  label="D_SOD-127"
  Group = -> [Part__Feature057]
  Origin = -> Origin136
  Placement = pos=(5.85,15.82,1.05) rot=(0,0,-1;1.5708rad)
FEATURE [Part::Feature] Part__Feature058  label="SOLID012"
  shape: bbox 7 x 7 x 0.77 mm, 302 faces (baked)
FEATURE [App::Part] QFN_48_1EP_7x7mm_P0_5mm_EP5_15x5_15mm001  label="QFN-48-1EP_7x7mm_P0.5mm_EP5.15x5.15mm001"
  Group = -> [Part__Feature058]
  Origin = -> Origin137
  Placement = pos=(17.7737,29.6588,1.05) rot=(0,0,-1;1.5708rad)
FEATURE [Part::Feature] Part__Feature059  label="SOLID013"
  shape: bbox 6.652 x 4.89 x 2.436 mm, 452 faces (baked)
FEATURE [App::Part] Button004
  Group = -> [Part__Feature059]
  Origin = -> Origin138
  Placement = pos=(2.48,8.73,1.05) rot=(0,0,-1;1.5708rad)
FEATURE [Part::Feature] Part__Feature060  label="SOLID014"
  shape: bbox 6.652 x 4.89 x 2.436 mm, 452 faces (baked)
FEATURE [App::Part] Button005
  Group = -> [Part__Feature060]
  Origin = -> Origin139
  Placement = pos=(31.32,10.53,1.05) rot=(0,0,1;1.5708rad)
FEATURE [Part::Feature] Part__Feature061  label="SOLID015"
  shape: bbox 3.8 x 1.6 x 1.25 mm, 67 faces (baked)
FEATURE [App::Part] D_SOD_123005  label="D_SOD-128"
  Group = -> [Part__Feature061]
  Origin = -> Origin140
  Placement = pos=(3.55,15.82,1.05) rot=(0,0,-1;1.5708rad)
FEATURE [Part::Feature] Part__Feature062  label="SOLID016"
  shape: bbox 7.65 x 5.2 x 3.4 mm, 136 faces (baked)
FEATURE [App::Part] Molex_PicoBlade_53261_0271_1x02_1MP_P1_25mm_Horizontal001  label="Molex_PicoBlade_53261-0271_1x02-1MP_P1.25mm_Horizontal001"
  Group = -> [Part__Feature062]
  Origin = -> Origin141
  Placement = pos=(28.63,31.39,1.05) rot=(0,0,-1;1.5708rad)
FEATURE [Part::Feature] Part__Feature063  label="SOLID017"
  shape: bbox 6.652 x 4.89 x 2.436 mm, 452 faces (baked)
FEATURE [App::Part] Button006
  Group = -> [Part__Feature063]
  Origin = -> Origin142
  Placement = pos=(31.32,37.23,1.05) rot=(0,0,1;1.5708rad)
FEATURE [Part::Feature] Part__Feature064  label="SOLID018"
  shape: bbox 6.652 x 4.89 x 2.436 mm, 452 faces (baked)
FEATURE [App::Part] Button007
  Group = -> [Part__Feature064]
  Origin = -> Origin143
  Placement = pos=(2.48,35.43,1.05) rot=(0,0,-1;1.5708rad)
FEATURE [Part::Feature] Part__Feature065  label="COMPOUND001"
  shape: bbox 16.31 x 5.857 x 2.117 mm, 1280 faces, 17 solids (baked)
FEATURE [App::Part] FPC_24001  label="FPC-025"
  Group = -> [Part__Feature065]
  Origin = -> Origin144
  Placement = pos=(11.025,19.09,1.05) rot=(0,0,1;0rad)
FEATURE [Part::Feature] Part__Feature066  label="COMPOUND002"
  shape: bbox 13 x 10 x 2.5 mm, 15 faces, 3 solids (baked)
FEATURE [App::Part] PagerMotor001
  Group = -> [Part__Feature066]
  Origin = -> Origin145
  Placement = pos=(5.45,22.955,4.55) rot=(0.819152,-0.573576,0;3.14159rad)
FEATURE [Part::Feature] Part__Feature067  label="SOLID019"
  shape: bbox 7.981 x 5.421 x 2.94 mm, 484 faces (baked)
FEATURE [App::Part] USB_Micro_B_Molex_47346_0001001  label="USB_Micro-B_Molex_47346-0002"
  Group = -> [Part__Feature067]
  Origin = -> Origin146
  Placement = pos=(31.38,22.43,1.05) rot=(0,0,1;1.5708rad)
FEATURE [Part::Feature] Part__Feature068  label="SOLID020"
  shape: bbox 3 x 2.9 x 0.6 mm, 74 faces (baked)
FEATURE [App::Part] DFN_10_1EP_3x3mm_P0_5mm_EP1_75x2_7mm  label="DFN-10-1EP_3x3mm_P0.5mm_EP1.75x2.7mm"
  Group = -> [Part__Feature068]
  Origin = -> Origin147
  Placement = pos=(11.76,32.64,1.05) rot=(0,0,-1;1.5708rad)
FEATURE [Part::Feature] Part__Feature069  label="COMPOUND003"
  shape: bbox 37.16 x 32.08 x 2.7 mm, 85 faces, 2 solids (baked)
FEATURE [App::Part] Display001
  Group = -> [Part__Feature069]
  Origin = -> Origin148
  Placement = pos=(16.89,23.15,-0.05) rot=(0.707107,0.707107,0;3.14159rad)
FEATURE [Part::Feature] Part__Feature070  label="Watchy PCB"
  shape: bbox 33.8 x 37.96 x 1 mm, 34 faces (baked)
FEATURE [PartDesign::ShapeBinder] ShapeBinder006
  Support = -> [Part__Feature070]
  TraceSupport = false
FEATURE [Sketcher::SketchObject] Sketch030
  ExternalGeometry = -> [ShapeBinder005,ShapeBinder006]
  FullyConstrained = true
  MapMode = 5
  Placement = pos=(0,0,-2.3) rot=(1,0,0;3.14159rad)
  Support = -> [ShapeBinder004]
  sketch-geometry (4):
    g0: LineSegment StartX=-1.8 StartY=-2.2 StartZ=0 EndX=35.6 EndY=-2.2 EndZ=0
    g1: LineSegment StartX=35.6 StartY=-2.2 StartZ=0 EndX=35.6 EndY=-43.76 EndZ=0
    g2: LineSegment StartX=35.6 StartY=-43.76 StartZ=0 EndX=-1.8 EndY=-43.76 EndZ=0
    g3: LineSegment StartX=-1.8 StartY=-43.76 StartZ=0 EndX=-1.8 EndY=-2.2 EndZ=0
  constraints (12):
    c: Coincident(g0,g1)
    c: Coincident(g1,g2)
    c: Coincident(g2,g3)
    c: Coincident(g3,g0)
    c: Horizontal(g0)
    c: Horizontal(g2)
    c: Vertical(g1)
    c: Vertical(g3)
    c: DistanceX(g0,g-8) = 1.8
    c: DistanceX(g-7,g1) = 1.8
    c: DistanceY(g1,g-7) = 1.8
    c: DistanceY(g-8,g0) = 1.8
FEATURE [PartDesign::Pad] Pad023
  Direction = (0,0,-1)
  Length = 9
  Length2 = 10
  Placement = pos=(0,0,-0.8) rot=(0,0,1;0rad)
  Profile = -> Sketch030
  ReferenceAxis = -> Sketch030 [N_Axis]
  Reversed = true
  Type = 0
FEATURE [Sketcher::SketchObject] Sketch031
  ExternalGeometry = -> [ShapeBinder005]
  FullyConstrained = true
  MapMode = 5
  Placement = pos=(0,0,-2.3) rot=(1,0,0;3.14159rad)
  Support = -> [Pad023]
  sketch-geometry (4):
    g0: LineSegment StartX=2.8 StartY=-12.1 StartZ=0 EndX=31.2 EndY=-12.1 EndZ=0
    g1: LineSegment StartX=31.2 StartY=-12.1 StartZ=0 EndX=31.2 EndY=-39.5 EndZ=0
    g2: LineSegment StartX=31.2 StartY=-39.5 StartZ=0 EndX=2.8 EndY=-39.5 EndZ=0
    g3: LineSegment StartX=2.8 StartY=-39.5 StartZ=0 EndX=2.8 EndY=-12.1 EndZ=0
  constraints (12):
    c: Coincident(g0,g1)
    c: Coincident(g1,g2)
    c: Coincident(g2,g3)
    c: Coincident(g3,g0)
    c: Horizontal(g0)
    c: Horizontal(g2)
    c: Vertical(g1)
    c: Vertical(g3)
    c: DistanceY(g-3,g0) = 0.2
    c: DistanceY(g1,g-4) = 0.2
    c: DistanceX(g2,g-4) = 0.2
    c: DistanceX(g-3,g0) = 0.2
FEATURE [PartDesign::Pocket] Pocket016
  BaseFeature = -> Pad023
  Direction = (0,0,1)
  Length = 0.8
  Length2 = 5
  Placement = pos=(0,0,-0.8) rot=(0,0,1;0rad)
  Profile = -> Sketch031
  ReferenceAxis = -> Sketch031 [N_Axis]
  Type = 0
FEATURE [Sketcher::SketchObject] Sketch032
  ExternalGeometry = -> [ShapeBinder006]
  FullyConstrained = true
  MapMode = 5
  Placement = pos=(0,0,6.7) rot=(0,0,1;0rad)
  Support = -> [Pocket016]
  sketch-geometry (4):
    g0: LineSegment StartX=-0.2 StartY=42.16 StartZ=0 EndX=34 EndY=42.16 EndZ=0
    g1: LineSegment StartX=34 StartY=42.16 StartZ=0 EndX=34 EndY=3.8 EndZ=0
    g2: LineSegment StartX=34 StartY=3.8 StartZ=0 EndX=-0.2 EndY=3.8 EndZ=0
    g3: LineSegment StartX=-0.2 StartY=3.8 StartZ=0 EndX=-0.2 EndY=42.16 EndZ=0
  constraints (12):
    c: Coincident(g0,g1)
    c: Coincident(g1,g2)
    c: Coincident(g2,g3)
    c: Coincident(g3,g0)
    c: Horizontal(g0)
    c: Horizontal(g2)
    c: Vertical(g1)
    c: Vertical(g3)
    c: DistanceX(g0,g-4) = 0.2
    c: DistanceY(g-4,g0) = 0.2
    c: DistanceY(g1,g-3) = 0.2
    c: DistanceX(g-3,g1) = 0.2
FEATURE [PartDesign::Pocket] Pocket017
  BaseFeature = -> Pocket016
  Direction = (0,0,-1)
  Length = 8.2
  Length2 = 5
  Placement = pos=(0,0,-0.8) rot=(0,0,1;0rad)
  Profile = -> Sketch032
  ReferenceAxis = -> Sketch032 [N_Axis]
  Type = 0
FEATURE [Sketcher::SketchObject] Sketch033
  ExternalGeometry = -> [ShapeBinder006]
  FullyConstrained = true
  MapMode = 5
  Placement = pos=(0,0,6.7) rot=(0,0,1;0rad)
  Support = -> [Pocket017]
  sketch-geometry (20):
    g0: LineSegment StartX=33.8 StartY=10.93 StartZ=0 EndX=34.7 EndY=10.93 EndZ=0
    g1: LineSegment StartX=34.7 StartY=10.93 StartZ=0 EndX=34.7 EndY=8.33 EndZ=0
    g2: LineSegment StartX=34.7 StartY=8.33 StartZ=0 EndX=33.8 EndY=8.33 EndZ=0
    g3: LineSegment StartX=33.8 StartY=8.33 StartZ=0 EndX=33.8 EndY=10.93 EndZ=0
    g4: GeomPoint X=34.25 Y=9.63 Z=0
    g5: LineSegment StartX=33.8 StartY=37.63 StartZ=0 EndX=34.7 EndY=37.63 EndZ=0
    g6: LineSegment StartX=34.7 StartY=37.63 StartZ=0 EndX=34.7 EndY=35.03 EndZ=0
    g7: LineSegment StartX=34.7 StartY=35.03 StartZ=0 EndX=33.8 EndY=35.03 EndZ=0
    g8: LineSegment StartX=33.8 StartY=35.03 StartZ=0 EndX=33.8 EndY=37.63 EndZ=0
    g9: LineSegment StartX=-0.9 StartY=10.93 StartZ=0 EndX=-1e-12 EndY=10.93 EndZ=0
    g10: LineSegment StartX=-1e-12 StartY=10.93 StartZ=0 EndX=-1e-12 EndY=8.33 EndZ=0
    g11: LineSegment StartX=-1e-12 StartY=8.33 StartZ=0 EndX=-0.9 EndY=8.33 EndZ=0
    g12: LineSegment StartX=-0.9 StartY=8.33 StartZ=0 EndX=-0.9 EndY=10.93 EndZ=0
    g13: LineSegment StartX=-0.9 StartY=37.63 StartZ=0 EndX=9.9463e-12 EndY=37.63 EndZ=0
    g14: LineSegment StartX=9.9463e-12 StartY=37.63 StartZ=0 EndX=9.9463e-12 EndY=35.03 EndZ=0
    g15: LineSegment StartX=9.9463e-12 StartY=35.03 StartZ=0 EndX=-0.9 EndY=35.03 EndZ=0
    g16: LineSegment StartX=-0.9 StartY=35.03 StartZ=0 EndX=-0.9 EndY=37.63 EndZ=0
    g17: GeomPoint X=34.25 Y=36.33 Z=0
    g18: GeomPoint X=-0.45 Y=9.63 Z=0
    g19: GeomPoint X=-0.45 Y=36.33 Z=0
  constraints (52):
    c: Coincident(g0,g1)
    c: Coincident(g1,g2)
    c: Coincident(g2,g3)
    c: Coincident(g3,g0)
    c: Horizontal(g0)
    c: Horizontal(g2)
    c: Vertical(g1)
    c: Vertical(g3)
    c: DistanceX(g2,g2) = 0.9
    c: DistanceY(g1,g1) = 2.6
    c: Symmetric(g0,g2,g4)
    c: Coincident(g5,g6)
    c: Coincident(g6,g7)
    c: Coincident(g7,g8)
    c: Coincident(g8,g5)
    c: Horizontal(g5)
    c: Horizontal(g7)
    c: Vertical(g6)
    c: Vertical(g8)
    c: Coincident(g9,g10)
    c: Coincident(g10,g11)
    c: Coincident(g11,g12)
    c: Coincident(g12,g9)
    c: Horizontal(g9)
    c: Horizontal(g11)
    c: Vertical(g10)
    c: Vertical(g12)
    c: Coincident(g13,g14)
    c: Coincident(g14,g15)
    c: Coincident(g15,g16)
    c: Coincident(g16,g13)
    c: Horizontal(g13)
    c: Horizontal(g15)
    c: Vertical(g14)
    c: Vertical(g16)
    c: Equal(g5,g0)
    c: Equal(g9,g5)
    c: Equal(g13,g9)
    c: Equal(g6,g1)
    c: Equal(g10,g6)
    c: Equal(g10,g14)
    c: Symmetric(g5,g7,g17)
    c: Symmetric(g9,g11,g18)
    c: Symmetric(g13,g15,g19)
    c: DistanceY(g19,g-4) = 5.63
    c: DistanceY(g17,g-3) = 5.63
    c: DistanceY(g-3,g4) = 5.63
    c: DistanceY(g-4,g18) = 5.63
    c: PointOnObject(g10,g-4)
    c: PointOnObject(g14,g-4)
    c: PointOnObject(g7,g-3)
    c: PointOnObject(g2,g-3)
FEATURE [PartDesign::Pocket] Pocket018
  BaseFeature = -> Pocket017
  Direction = (0,0,-1)
  Length = 8
  Length2 = 5
  Placement = pos=(0,0,-0.8) rot=(0,0,1;0rad)
  Profile = -> Sketch033
  ReferenceAxis = -> Sketch033 [N_Axis]
  Type = 0
FEATURE [App::Part] Watchy_1  label="Watchy 1"
  Group = -> [QFN_24_1EP_4x4mm_P0_5mm_EP2_7x2_7mm001,D_SOD_123004,QFN_48_1EP_7x7mm_P0_5mm_EP5_15x5_15mm001,Button004,Button005,D_SOD_123005,Molex_PicoBlade_53261_0271_1x02_1MP_P1_25mm_Horizontal001,Button006,Button007,FPC_24001,PagerMotor001,USB_Micro_B_Molex_47346_0001001,DFN_10_1EP_3x3mm_P0_5mm_EP1_75x2_7mm,Display001,Part__Feature070]
  Origin = -> Origin149
FEATURE [Sketcher::SketchObject] Sketch034
  FullyConstrained = true
  MapMode = 5
  Placement = pos=(35.6,0,-0.8) rot=(0.57735,0.57735,0.57735;2.0944rad)
  Support = -> [Pocket018]
  sketch-geometry (4):
    g0: LineSegment StartX=18.18 StartY=4.79 StartZ=0 EndX=26.68 EndY=4.79 EndZ=0
    g1: LineSegment StartX=26.68 StartY=4.79 StartZ=0 EndX=26.68 EndY=1.39 EndZ=0
    g2: LineSegment StartX=26.68 StartY=1.39 StartZ=0 EndX=18.18 EndY=1.39 EndZ=0
    g3: LineSegment StartX=18.18 StartY=1.39 StartZ=0 EndX=18.18 EndY=4.79 EndZ=0
  constraints (12):
    c: Coincident(g0,g1)
    c: Coincident(g1,g2)
    c: Coincident(g2,g3)
    c: Coincident(g3,g0)
    c: Horizontal(g0)
    c: Horizontal(g2)
    c: Vertical(g1)
    c: Vertical(g3)
    c: DistanceX(g0,g0) = 8.5
    c: DistanceY(g1,g1) = 3.4
    c: DistanceX(g-1,g2) = 18.18
    c: DistanceY(g-1,g2) = 1.39
FEATURE [PartDesign::Pocket] Pocket019
  BaseFeature = -> Pocket018
  Direction = (-1,0,0)
  Length = 5
  Length2 = 5
  Placement = pos=(0,0,-0.8) rot=(0,0,1;0rad)
  Profile = -> Sketch034
  ReferenceAxis = -> Sketch034 [N_Axis]
  Type = 0
FEATURE [Sketcher::SketchObject] Sketch035
  ExternalGeometry = -> [ShapeBinder006]
  FullyConstrained = true
  MapMode = 5
  Placement = pos=(-1.8,0,-0.8) rot=(0.57735,-0.57735,-0.57735;2.0944rad)
  Support = -> [Pocket019]
  sketch-geometry (10):
    g0: LineSegment StartX=-6.625 StartY=4.05 StartZ=0 EndX=-12.625 EndY=4.05 EndZ=0
    g1: LineSegment StartX=-12.625 StartY=4.05 StartZ=0 EndX=-12.625 EndY=1.55 EndZ=0
    g2: LineSegment StartX=-12.625 StartY=1.55 StartZ=0 EndX=-6.625 EndY=1.55 EndZ=0
    g3: LineSegment StartX=-6.625 StartY=1.55 StartZ=0 EndX=-6.625 EndY=4.05 EndZ=0
    g4: GeomPoint X=-9.625 Y=2.8 Z=0
    g5: LineSegment StartX=-39.335 StartY=4.05 StartZ=0 EndX=-33.335 EndY=4.05 EndZ=0
    g6: LineSegment StartX=-33.335 StartY=4.05 StartZ=0 EndX=-33.335 EndY=1.55 EndZ=0
    g7: LineSegment StartX=-33.335 StartY=1.55 StartZ=0 EndX=-39.335 EndY=1.55 EndZ=0
    g8: LineSegment StartX=-39.335 StartY=1.55 StartZ=0 EndX=-39.335 EndY=4.05 EndZ=0
    g9: GeomPoint X=-36.335 Y=2.8 Z=0
  constraints (26):
    c: Coincident(g0,g1)
    c: Coincident(g1,g2)
    c: Coincident(g2,g3)
    c: Coincident(g3,g0)
    c: Horizontal(g0)
    c: Horizontal(g2)
    c: Vertical(g1)
    c: Vertical(g3)
    c: Symmetric(g0,g1,g4)
    c: DistanceX(g4,g-3) = 5.625
    c: DistanceY(g-3,g4) = 1
    c: DistanceX(g0,g0) = 6
    c: DistanceY(g3,g3) = 2.5
    c: Coincident(g5,g6)
    c: Coincident(g6,g7)
    c: Coincident(g7,g8)
    c: Coincident(g8,g5)
    c: Horizontal(g5)
    c: Horizontal(g7)
    c: Vertical(g6)
    c: Vertical(g8)
    c: Equal(g0,g5)
    c: Equal(g3,g6)
    c: Symmetric(g5,g6,g9)
    c: DistanceX(g-3,g9) = 5.625
    c: DistanceY(g-3,g9) = 1
FEATURE [PartDesign::Pad] Pad024
  BaseFeature = -> Pocket019
  Direction = (-1,0,0)
  Length = 2
  Length2 = 10
  Placement = pos=(0,0,-0.8) rot=(0,0,1;0rad)
  Profile = -> Sketch035
  ReferenceAxis = -> Sketch035 [N_Axis]
  Type = 0
FEATURE [Sketcher::SketchObject] Sketch036
  ExternalGeometry = -> [ShapeBinder006]
  FullyConstrained = true
  MapMode = 5
  Placement = pos=(35.6,0,-0.8) rot=(0.57735,0.57735,0.57735;2.0944rad)
  Support = -> [Pad024]
  sketch-geometry (10):
    g0: LineSegment StartX=6.625 StartY=4.05 StartZ=0 EndX=12.625 EndY=4.05 EndZ=0
    g1: LineSegment StartX=12.625 StartY=4.05 StartZ=0 EndX=12.625 EndY=1.55 EndZ=0
    g2: LineSegment StartX=12.625 StartY=1.55 StartZ=0 EndX=6.625 EndY=1.55 EndZ=0
    g3: LineSegment StartX=6.625 StartY=1.55 StartZ=0 EndX=6.625 EndY=4.05 EndZ=0
    g4: LineSegment StartX=33.335 StartY=4.05 StartZ=0 EndX=39.335 EndY=4.05 EndZ=0
    g5: LineSegment StartX=39.335 StartY=4.05 StartZ=0 EndX=39.335 EndY=1.55 EndZ=0
    g6: LineSegment StartX=39.335 StartY=1.55 StartZ=0 EndX=33.335 EndY=1.55 EndZ=0
    g7: LineSegment StartX=33.335 StartY=1.55 StartZ=0 EndX=33.335 EndY=4.05 EndZ=0
    g8: GeomPoint X=9.625 Y=2.8 Z=0
    g9: GeomPoint X=36.335 Y=2.8 Z=0
  constraints (26):
    c: Coincident(g0,g1)
    c: Coincident(g1,g2)
    c: Coincident(g2,g3)
    c: Coincident(g3,g0)
    c: Horizontal(g0)
    c: Horizontal(g2)
    c: Vertical(g1)
    c: Vertical(g3)
    c: Coincident(g4,g5)
    c: Coincident(g5,g6)
    c: Coincident(g6,g7)
    c: Coincident(g7,g4)
    c: Horizontal(g4)
    c: Horizontal(g6)
    c: Vertical(g5)
    c: Vertical(g7)
    c: Symmetric(g0,g1,g8)
    c: Symmetric(g4,g5,g9)
    c: DistanceX(g4,g4) = 6
    c: DistanceY(g5,g5) = 2.5
    c: Equal(g5,g1)
    c: Equal(g4,g0)
    c: DistanceX(g-3,g8) = 5.625
    c: DistanceX(g9,g-3) = 5.625
    c: DistanceY(g-3,g8) = 1
    c: DistanceY(g-3,g9) = 1
FEATURE [PartDesign::Pad] Pad025
  BaseFeature = -> Pad024
  Direction = (1,0,0)
  Length = 2
  Length2 = 10
  Placement = pos=(0,0,-0.8) rot=(0,0,1;0rad)
  Profile = -> Sketch036
  ReferenceAxis = -> Sketch036 [N_Axis]
  Type = 0
FEATURE [Sketcher::SketchObject] Sketch037
  ExternalGeometry = -> [ShapeBinder006]
  FullyConstrained = true
  MapMode = 5
  Placement = pos=(0,42.16,-0.8) rot=(1,0,0;1.5708rad)
  Support = -> [Pad025]
  sketch-geometry (6):
    g0: LineSegment StartX=6.9 StartY=2.8 StartZ=0 EndX=26.9 EndY=2.8 EndZ=0
    g1: LineSegment StartX=26.9 StartY=2.8 StartZ=0 EndX=26.9 EndY=1.8 EndZ=0
    g2: LineSegment StartX=26.9 StartY=1.8 StartZ=0 EndX=6.9 EndY=1.8 EndZ=0
    g3: LineSegment StartX=6.9 StartY=1.8 StartZ=0 EndX=6.9 EndY=2.8 EndZ=0
    g4: LineSegment StartX=0 StartY=1.8 StartZ=0 EndX=33.8 EndY=1.8 EndZ=0
    g5: GeomPoint X=16.9 Y=1.8 Z=0
  constraints (14):
    c: Coincident(g0,g1)
    c: Coincident(g1,g2)
    c: Coincident(g2,g3)
    c: Coincident(g3,g0)
    c: Horizontal(g0)
    c: Horizontal(g2)
    c: Vertical(g1)
    c: Vertical(g3)
    c: DistanceY(g1,g1) = 1
    c: DistanceX(g0,g0) = 20
    c: Coincident(g4,g-4)
    c: Coincident(g4,g-3)
    c: Symmetric(g2,g1,g5)
    c: Symmetric(g4,g4,g5)
FEATURE [PartDesign::Pad] Pad026
  BaseFeature = -> Pad025
  Direction = (0,-1,2e-16)
  Length = 1
  Length2 = 10
  Placement = pos=(0,0,-0.8) rot=(0,0,1;0rad)
  Profile = -> Sketch037
  ReferenceAxis = -> Sketch037 [N_Axis]
  Type = 0
FEATURE [Sketcher::SketchObject] Sketch038
  ExternalGeometry = -> [ShapeBinder006]
  FullyConstrained = true
  MapMode = 5
  Placement = pos=(0,3.8,-0.8) rot=(0,0.707107,0.707107;3.14159rad)
  Support = -> [Pad026]
  sketch-geometry (9):
    g0: LineSegment StartX=-33.8 StartY=1.8 StartZ=0 EndX=0 EndY=1.8 EndZ=0
    g1: LineSegment StartX=-31.8 StartY=1.8 StartZ=0 EndX=-26.8 EndY=1.8 EndZ=0
    g2: LineSegment StartX=-26.8 StartY=1.8 StartZ=0 EndX=-26.8 EndY=2.8 EndZ=0
    g3: LineSegment StartX=-26.8 StartY=2.8 StartZ=0 EndX=-31.8 EndY=2.8 EndZ=0
    g4: LineSegment StartX=-31.8 StartY=2.8 StartZ=0 EndX=-31.8 EndY=1.8 EndZ=0
    g5: LineSegment StartX=-7 StartY=1.8 StartZ=0 EndX=-2 EndY=1.8 EndZ=0
    g6: LineSegment StartX=-2 StartY=1.8 StartZ=0 EndX=-2 EndY=2.8 EndZ=0
    g7: LineSegment StartX=-2 StartY=2.8 StartZ=0 EndX=-7 EndY=2.8 EndZ=0
    g8: LineSegment StartX=-7 StartY=2.8 StartZ=0 EndX=-7 EndY=1.8 EndZ=0
  constraints (26):
    c: Coincident(g0,g-4)
    c: Coincident(g0,g-3)
    c: Coincident(g1,g2)
    c: Coincident(g2,g3)
    c: Coincident(g3,g4)
    c: Coincident(g4,g1)
    c: Horizontal(g1)
    c: Horizontal(g3)
    c: Vertical(g2)
    c: Vertical(g4)
    c: PointOnObject(g1,g0)
    c: Coincident(g5,g6)
    c: Coincident(g6,g7)
    c: Coincident(g7,g8)
    c: Coincident(g8,g5)
    c: Horizontal(g5)
    c: Horizontal(g7)
    c: Vertical(g6)
    c: Vertical(g8)
    c: PointOnObject(g5,g0)
    c: Equal(g2,g8)
    c: Equal(g3,g7)
    c: DistanceY(g2,g2) = 1
    c: DistanceX(g3,g3) = 5
    c: DistanceX(g0,g1) = 2
    c: DistanceX(g5,g0) = 2
FEATURE [PartDesign::Pad] Pad027
  BaseFeature = -> Pad026
  Direction = (0,1,-2e-16)
  Length = 1
  Length2 = 10
  Placement = pos=(0,0,-0.8) rot=(0,0,1;0rad)
  Profile = -> Sketch038
  ReferenceAxis = -> Sketch038 [N_Axis]
  Type = 0
FEATURE [Sketcher::SketchObject] Sketch039
  ExternalGeometry = -> [Pad027]
  FullyConstrained = true
  MapMode = 5
  Placement = pos=(0,42.16,-0.8) rot=(1,0,0;1.5708rad)
  Support = -> [Pad027]
  sketch-geometry (5):
    g0: LineSegment StartX=1.9 StartY=6.5 StartZ=0 EndX=31.9 EndY=6.5 EndZ=0
    g1: LineSegment StartX=31.9 StartY=6.5 StartZ=0 EndX=31.9 EndY=5.5 EndZ=0
    g2: LineSegment StartX=31.9 StartY=5.5 StartZ=0 EndX=1.9 EndY=5.5 EndZ=0
    g3: LineSegment StartX=1.9 StartY=5.5 StartZ=0 EndX=1.9 EndY=6.5 EndZ=0
    g4: GeomPoint X=16.9 Y=6 Z=0
  constraints (13):
    c: Coincident(g0,g1)
    c: Coincident(g1,g2)
    c: Coincident(g2,g3)
    c: Coincident(g3,g0)
    c: Horizontal(g0)
    c: Horizontal(g2)
    c: Vertical(g1)
    c: Vertical(g3)
    c: DistanceY(g1,g1) = 1
    c: DistanceX(g0,g0) = 30
    c: DistanceY(g0,g-3) = 1
    c: Symmetric(g2,g0,g4)
    c: DistanceX(g-3,g0) = 2.1
FEATURE [PartDesign::Pocket] Pocket020
  BaseFeature = -> Pad027
  Direction = (0,1,-2e-16)
  Length = 1
  Length2 = 5
  Placement = pos=(0,0,-0.8) rot=(0,0,1;0rad)
  Profile = -> Sketch039
  ReferenceAxis = -> Sketch039 [N_Axis]
  Type = 0
FEATURE [Sketcher::SketchObject] Sketch040
  ExternalGeometry = -> [Pocket020]
  FullyConstrained = true
  MapMode = 5
  Placement = pos=(0,3.8,-0.8) rot=(0,0.707107,0.707107;3.14159rad)
  Support = -> [Pocket020]
  sketch-geometry (4):
    g0: LineSegment StartX=-31.9 StartY=6.5 StartZ=0 EndX=-1.9 EndY=6.5 EndZ=0
    g1: LineSegment StartX=-1.9 StartY=6.5 StartZ=0 EndX=-1.9 EndY=5.5 EndZ=0
    g2: LineSegment StartX=-1.9 StartY=5.5 StartZ=0 EndX=-31.9 EndY=5.5 EndZ=0
    g3: LineSegment StartX=-31.9 StartY=5.5 StartZ=0 EndX=-31.9 EndY=6.5 EndZ=0
  constraints (12):
    c: Coincident(g0,g1)
    c: Coincident(g1,g2)
    c: Coincident(g2,g3)
    c: Coincident(g3,g0)
    c: Horizontal(g0)
    c: Horizontal(g2)
    c: Vertical(g1)
    c: Vertical(g3)
    c: DistanceX(g0,g0) = 30
    c: DistanceY(g1,g1) = 1
    c: DistanceX(g-3,g0) = 2.1
    c: DistanceY(g0,g-3) = 1
FEATURE [PartDesign::Pocket] Pocket021
  BaseFeature = -> Pocket020
  Direction = (0,-1,2e-16)
  Length = 1
  Length2 = 5
  Placement = pos=(0,0,-0.8) rot=(0,0,1;0rad)
  Profile = -> Sketch040
  ReferenceAxis = -> Sketch040 [N_Axis]
  Type = 0
FEATURE [Sketcher::SketchObject] Sketch041
  ExternalGeometry = -> [Pocket021]
  FullyConstrained = true
  MapMode = 5
  Placement = pos=(34,0,-0.8) rot=(0.57735,-0.57735,-0.57735;2.0944rad)
  Support = -> [Pocket021]
  sketch-geometry (4):
    g0: LineSegment StartX=-32.98 StartY=6.5 StartZ=0 EndX=-12.98 EndY=6.5 EndZ=0
    g1: LineSegment StartX=-12.98 StartY=6.5 StartZ=0 EndX=-12.98 EndY=5.5 EndZ=0
    g2: LineSegment StartX=-12.98 StartY=5.5 StartZ=0 EndX=-32.98 EndY=5.5 EndZ=0
    g3: LineSegment StartX=-32.98 StartY=5.5 StartZ=0 EndX=-32.98 EndY=6.5 EndZ=0
  constraints (12):
    c: Coincident(g0,g1)
    c: Coincident(g1,g2)
    c: Coincident(g2,g3)
    c: Coincident(g3,g0)
    c: Horizontal(g0)
    c: Horizontal(g2)
    c: Vertical(g1)
    c: Vertical(g3)
    c: DistanceY(g1,g1) = 1
    c: DistanceX(g0,g0) = 20
    c: DistanceY(g0,g-3) = 1
    c: DistanceX(g-3,g0) = 2.05
FEATURE [PartDesign::Pocket] Pocket022
  BaseFeature = -> Pocket021
  Direction = (1,0,0)
  Length = 1
  Length2 = 5
  Placement = pos=(0,0,-0.8) rot=(0,0,1;0rad)
  Profile = -> Sketch041
  ReferenceAxis = -> Sketch041 [N_Axis]
  Type = 0
FEATURE [Sketcher::SketchObject] Sketch042
  ExternalGeometry = -> [Pocket022]
  FullyConstrained = true
  MapMode = 5
  Placement = pos=(-0.2,0,-0.8) rot=(0.57735,0.57735,0.57735;2.0944rad)
  Support = -> [Pocket022]
  sketch-geometry (4):
    g0: LineSegment StartX=12.98 StartY=6.5 StartZ=0 EndX=32.98 EndY=6.5 EndZ=0
    g1: LineSegment StartX=32.98 StartY=6.5 StartZ=0 EndX=32.98 EndY=5.5 EndZ=0
    g2: LineSegment StartX=32.98 StartY=5.5 StartZ=0 EndX=12.98 EndY=5.5 EndZ=0
    g3: LineSegment StartX=12.98 StartY=5.5 StartZ=0 EndX=12.98 EndY=6.5 EndZ=0
  constraints (12):
    c: Coincident(g0,g1)
    c: Coincident(g1,g2)
    c: Coincident(g2,g3)
    c: Coincident(g3,g0)
    c: Horizontal(g0)
    c: Horizontal(g2)
    c: Vertical(g1)
    c: Vertical(g3)
    c: DistanceX(g0,g0) = 20
    c: DistanceY(g3,g3) = 1
    c: DistanceY(g0,g-3) = 1
    c: DistanceX(g0,g-3) = 2.05
FEATURE [PartDesign::Pocket] Pocket023
  BaseFeature = -> Pocket022
  Direction = (-1,0,0)
  Length = 1
  Length2 = 5
  Placement = pos=(0,0,-0.8) rot=(0,0,1;0rad)
  Profile = -> Sketch042
  ReferenceAxis = -> Sketch042 [N_Axis]
  Type = 0
FEATURE [PartDesign::Body] Body006  label="Case-Top-X"
  Group = -> [ShapeBinder004,Sketch030,ShapeBinder005,ShapeBinder006,Pad023,Sketch031,Pocket016,Sketch032,Pocket017,Sketch033,Pocket018,Sketch034,Pocket019,Sketch035,Pad024,Sketch036,Pad025,Sketch037,Pad026,Sketch038,Pad027,Sketch039,Pocket020,Sketch040,Pocket021,Sketch041,Pocket022,Sketch042,Pocket023]
  Origin = -> Origin134
  Tip = -> Pocket023
FEATURE [PartDesign::Plane] DatumPlane003
  Length = 73.5102
  MapMode = 5
  Placement = pos=(0,0,6.7) rot=(0,0,1;0rad)
  ResizeMode = 0
  Width = 81.6702
FEATURE [PartDesign::ShapeBinder] ShapeBinder007
  Placement = pos=(0,0,-0.8) rot=(0,0,1;0rad)
  Support = -> [Pocket023]
  TraceSupport = false
FEATURE [Sketcher::SketchObject] Sketch043
  ExternalGeometry = -> [ShapeBinder007]
  FullyConstrained = true
  MapMode = 5
  Placement = pos=(0,0,6.7) rot=(0,0,1;0rad)
  Support = -> [DatumPlane003]
  sketch-geometry (4):
    g0: LineSegment StartX=-1.8 StartY=43.76 StartZ=0 EndX=35.6 EndY=43.76 EndZ=0
    g1: LineSegment StartX=35.6 StartY=43.76 StartZ=0 EndX=35.6 EndY=2.2 EndZ=0
    g2: LineSegment StartX=35.6 StartY=2.2 StartZ=0 EndX=-1.8 EndY=2.2 EndZ=0
    g3: LineSegment StartX=-1.8 StartY=2.2 StartZ=0 EndX=-1.8 EndY=43.76 EndZ=0
  constraints (10):
    c: Coincident(g0,g1)
    c: Coincident(g1,g2)
    c: Coincident(g2,g3)
    c: Coincident(g3,g0)
    c: Horizontal(g0)
    c: Horizontal(g2)
    c: Vertical(g1)
    c: Vertical(g3)
    c: Coincident(g0,g-3)
    c: Coincident(g1,g-4)
FEATURE [PartDesign::Pad] Pad028
  Direction = (0,0,1)
  Length = 4
  Length2 = 10
  Placement = pos=(0,0,6.7) rot=(0,0,1;0rad)
  Profile = -> Sketch043
  ReferenceAxis = -> Sketch043 [N_Axis]
  Type = 0
FEATURE [Sketcher::SketchObject] Sketch044
  ExternalGeometry = -> [ShapeBinder007]
  FullyConstrained = true
  MapMode = 5
  Placement = pos=(0,0,6.7) rot=(1,0,0;3.14159rad)
  Support = -> [Pad028]
  sketch-geometry (4):
    g0: LineSegment StartX=-0.2 StartY=-3.8 StartZ=0 EndX=34 EndY=-3.8 EndZ=0
    g1: LineSegment StartX=34 StartY=-3.8 StartZ=0 EndX=34 EndY=-42.16 EndZ=0
    g2: LineSegment StartX=34 StartY=-42.16 StartZ=0 EndX=-0.2 EndY=-42.16 EndZ=0
    g3: LineSegment StartX=-0.2 StartY=-42.16 StartZ=0 EndX=-0.2 EndY=-3.8 EndZ=0
  constraints (10):
    c: Coincident(g0,g1)
    c: Coincident(g1,g2)
    c: Coincident(g2,g3)
    c: Coincident(g3,g0)
    c: Horizontal(g0)
    c: Horizontal(g2)
    c: Vertical(g1)
    c: Vertical(g3)
    c: Coincident(g0,g-3)
    c: Coincident(g1,g-4)
FEATURE [PartDesign::Pad] Pad029
  BaseFeature = -> Pad028
  Direction = (0,0,-1)
  Length = 2
  Length2 = 10
  Placement = pos=(0,0,6.7) rot=(0,0,1;0rad)
  Profile = -> Sketch044
  ReferenceAxis = -> Sketch044 [N_Axis]
  Type = 0
FEATURE [Sketcher::SketchObject] Sketch045
  ExternalGeometry = -> [Pad029]
  FullyConstrained = true
  MapMode = 5
  Placement = pos=(0,0,4.7) rot=(1,0,0;3.14159rad)
  Support = -> [Pad029]
  sketch-geometry (4):
    g0: LineSegment StartX=0.8 StartY=-4.8 StartZ=0 EndX=33 EndY=-4.8 EndZ=0
    g1: LineSegment StartX=33 StartY=-4.8 StartZ=0 EndX=33 EndY=-41.16 EndZ=0
    g2: LineSegment StartX=33 StartY=-41.16 StartZ=0 EndX=0.8 EndY=-41.16 EndZ=0
    g3: LineSegment StartX=0.8 StartY=-41.16 StartZ=0 EndX=0.8 EndY=-4.8 EndZ=0
  constraints (12):
    c: Coincident(g0,g1)
    c: Coincident(g1,g2)
    c: Coincident(g2,g3)
    c: Coincident(g3,g0)
    c: Horizontal(g0)
    c: Horizontal(g2)
    c: Vertical(g1)
    c: Vertical(g3)
    c: DistanceX(g-3,g0) = 1
    c: DistanceX(g1,g-4) = 1
    c: DistanceY(g-4,g1) = 1
    c: DistanceY(g0,g-3) = 1
FEATURE [PartDesign::Pocket] Pocket024
  BaseFeature = -> Pad029
  Direction = (0,0,1)
  Length = 5
  Length2 = 5
  Placement = pos=(0,0,6.7) rot=(0,0,1;0rad)
  Profile = -> Sketch045
  ReferenceAxis = -> Sketch045 [N_Axis]
  Type = 0
FEATURE [Sketcher::SketchObject] Sketch046
  ExternalGeometry = -> [Pocket024]
  FullyConstrained = true
  MapMode = 5
  Placement = pos=(0,42.16,6.7) rot=(0,0.707107,0.707107;3.14159rad)
  Support = -> [Pocket024]
  sketch-geometry (4):
    g0: LineSegment StartX=-34 StartY=-2 StartZ=0 EndX=0.2 EndY=-2 EndZ=0
    g1: LineSegment StartX=0.2 StartY=-2 StartZ=0 EndX=0.2 EndY=-1.2 EndZ=0
    g2: LineSegment StartX=0.2 StartY=-1.2 StartZ=0 EndX=-34 EndY=-1.2 EndZ=0
    g3: LineSegment StartX=-34 StartY=-1.2 StartZ=0 EndX=-34 EndY=-2 EndZ=0
  constraints (11):
    c: Coincident(g0,g1)
    c: Coincident(g1,g2)
    c: Coincident(g2,g3)
    c: Coincident(g3,g0)
    c: Horizontal(g0)
    c: Horizontal(g2)
    c: Vertical(g1)
    c: Vertical(g3)
    c: Coincident(g0,g-3)
    c: PointOnObject(g1,g-4)
    c: DistanceY(g0,g2) = 0.8
FEATURE [PartDesign::Pad] Pad030
  BaseFeature = -> Pocket024
  Direction = (0,1,-2e-16)
  Length = 0.8
  Length2 = 10
  Placement = pos=(0,0,6.7) rot=(0,0,1;0rad)
  Profile = -> Sketch046
  ReferenceAxis = -> Sketch046 [N_Axis]
  Type = 0
FEATURE [Sketcher::SketchObject] Sketch047
  FullyConstrained = true
  MapMode = 5
  Placement = pos=(-0.2,0,6.7) rot=(0.57735,-0.57735,-0.57735;2.0944rad)
  Support = -> [Pad030]
FEATURE [PartDesign::Body] Body007
  Group = -> [DatumPlane003,ShapeBinder007,Sketch043,Pad028,Sketch044,Pad029,Sketch045,Pocket024,Sketch046,Pad030,Sketch047]
  Origin = -> Origin150
  Tip = -> Pad030
